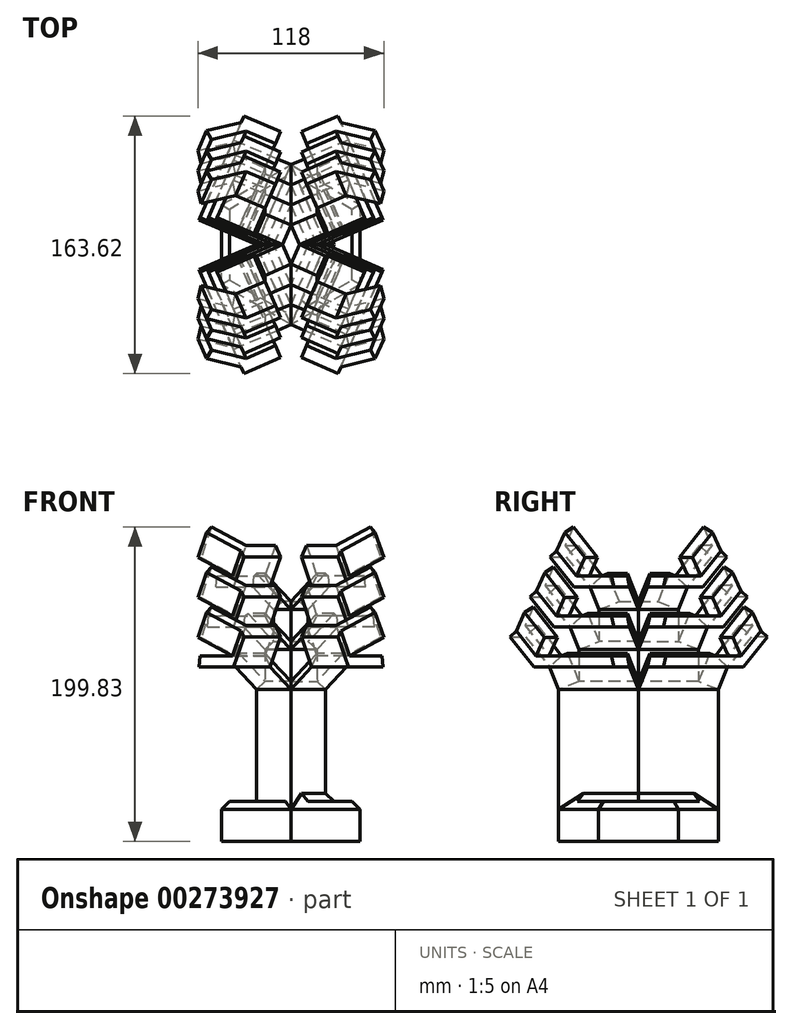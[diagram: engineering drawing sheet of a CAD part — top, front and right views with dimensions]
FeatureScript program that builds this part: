
annotation { "Feature Type Name" : "Feature", "Feature Type Description" : "" }
export const myFeature = defineFeature(function(context is Context, id is Id, definition is map)
    precondition{}
    {
        {
            var Q0;
            Q0=qCreatedBy(makeId("Top.planeOp"),FACE);
            var sketch = newSketch(context, id + "F0", { "sketchPlane" : qUnion([Q0])});
            skCircle(sketch, "E0.cCircle", {"center": v(0, 0) * mm, "radius": 43.95 * mm, "construction": true});
            skLineSegment(sketch, "E0.0", {"start": v(43.95, 25.37) * mm, "end": v(43.95, -25.37) * mm});
            skLineSegment(sketch, "E0.1", {"start": v(43.95, -25.37) * mm, "end": v(0, -50.74) * mm});
            skLineSegment(sketch, "E0.2", {"start": v(0, -50.74) * mm, "end": v(-43.95, -25.37) * mm});
            skLineSegment(sketch, "E0.3", {"start": v(-43.95, -25.37) * mm, "end": v(-43.95, 25.37) * mm});
            skLineSegment(sketch, "E0.4", {"start": v(-43.95, 25.37) * mm, "end": v(0, 50.74) * mm});
            skLineSegment(sketch, "E0.5", {"start": v(0, 50.74) * mm, "end": v(43.95, 25.37) * mm});
            skPoint(sketch, "E0.0.midPoint", {"position": v(43.95, 0) * mm});
            skLineSegment(sketch, "E1", {"start": v(-21.97, 0) * mm, "end": v(0, 0) * mm});
            skLineSegment(sketch, "E2", {"start": v(-21.97, 0) * mm, "end": v(0, -50.74) * mm});
            skLineSegment(sketch, "E3", {"start": v(0, 50.74) * mm, "end": v(-21.97, 0) * mm});
            skLineSegment(sketch, "E4", {"start": v(0, 0) * mm, "end": v(21.97, 0) * mm});
            skPoint(sketch, "E4.endSnap0", {"position": v(21.97, 38.06) * mm});
            skLineSegment(sketch, "E5", {"start": v(21.97, 0) * mm, "end": v(0, 50.74) * mm});
            skLineSegment(sketch, "E6", {"start": v(0, -50.74) * mm, "end": v(21.97, 0) * mm});
            skSolve(sketch);
        }
        {
            var Q0;
            Q0 = qSketchRegion(id + "F0", true);
            extrude(context, id + "F1", {"entities" : qUnion([Q0]), "depth" : 25.4 * mm});
        }
        {
            var Q0;
            Q0=makeQuery(id+"F1.opExtrude","CAP_FACE",FACE,{"disambiguationData":[OSD([sQuery(id+"F0.wireOp",EDGE,"E0.0"),sQuery(id+"F0.wireOp",EDGE,"E0.1"),sQuery(id+"F0.wireOp",EDGE,"E0.2"),sQuery(id+"F0.wireOp",EDGE,"E0.3"),sQuery(id+"F0.wireOp",EDGE,"E0.4"),sQuery(id+"F0.wireOp",EDGE,"E0.5")])],"isStart":false});
            var sketch = newSketch(context, id + "F2", { "sketchPlane" : qUnion([Q0])});
            skLineSegment(sketch, "E7", {"start": v(0, 50.74) * mm, "end": v(-21.97, 0) * mm});
            skPoint(sketch, "E7.endSnap0", {"position": v(-21.97, 38.06) * mm});
            skLineSegment(sketch, "E8", {"start": v(-21.97, 0) * mm, "end": v(0, -50.74) * mm});
            skLineSegment(sketch, "E9", {"start": v(0, -50.74) * mm, "end": v(21.97, 0) * mm});
            skPoint(sketch, "E9.endSnap0", {"position": v(21.97, -38.06) * mm});
            skLineSegment(sketch, "E10", {"start": v(21.97, 0) * mm, "end": v(0, 50.74) * mm});
            skSolve(sketch);
        }
        {
            var Q0;
            Q0 = qSketchRegion(id + "F2", true);
            extrude(context, id + "F3", {"entities" : qUnion([Q0]), "operationType" : NewBodyOperationType.ADD, "depth" : 25.4 * mm});
        }
        {
            var Q0;
            Q0=makeQuery(id+"F3.opExtrude","CAP_FACE",FACE,{"disambiguationData":[OSD([sQuery(id+"F2.wireOp",EDGE,"E7"),sQuery(id+"F2.wireOp",EDGE,"E8"),sQuery(id+"F2.wireOp",EDGE,"E9"),sQuery(id+"F2.wireOp",EDGE,"E10")])],"isStart":false});
            extrude(context, id + "F4", {"entities" : qUnion([Q0]), "operationType" : NewBodyOperationType.ADD, "depth" : 25.4 * mm});
        }
        {
            var Q0;
            Q0=makeQuery(id+"F4.opExtrude","CAP_FACE",FACE,{"disambiguationData":[OSD([sQuery(id+"F2.wireOp",EDGE,"E7"),sQuery(id+"F2.wireOp",EDGE,"E8"),sQuery(id+"F2.wireOp",EDGE,"E9"),sQuery(id+"F2.wireOp",EDGE,"E10")])],"isStart":false});
            extrude(context, id + "F5", {"entities" : qUnion([Q0]), "operationType" : NewBodyOperationType.ADD, "depth" : 25.4 * mm});
        }
        {
            var Q0;
            Q0=makeQuery(id+"F1.opExtrude","CAP_EDGE",EDGE,{"disambiguationData":[OSD([sQuery(id+"F0.wireOp",EDGE,"E0.0")])],"isStart":false});
            var Q1;
            Q1=makeQuery(id+"F1.opExtrude","CAP_EDGE",EDGE,{"disambiguationData":[OSD([sQuery(id+"F0.wireOp",EDGE,"E0.1")])],"isStart":false});
            var Q2;
            Q2=makeQuery(id+"F1.opExtrude","CAP_EDGE",EDGE,{"disambiguationData":[OSD([sQuery(id+"F0.wireOp",EDGE,"E0.5")])],"isStart":false});
            var Q3;
            Q3=makeQuery(id+"F1.opExtrude","CAP_EDGE",EDGE,{"disambiguationData":[OSD([sQuery(id+"F0.wireOp",EDGE,"E0.4")])],"isStart":false});
            var Q4;
            Q4=makeQuery(id+"F1.opExtrude","CAP_EDGE",EDGE,{"disambiguationData":[OSD([sQuery(id+"F0.wireOp",EDGE,"E0.3")])],"isStart":false});
            var Q5;
            Q5=makeQuery(id+"F1.opExtrude","CAP_EDGE",EDGE,{"disambiguationData":[OSD([sQuery(id+"F0.wireOp",EDGE,"E0.2")])],"isStart":false});
            chamfer(context, id + "F6", {"entities" : qUnion([Q0, Q1, Q2, Q3, Q4, Q5]), "width" : 5.08 * mm, "tangentPropagation" : true});
        }
        {
            var Q0;
            Q0=makeQuery(id+"F3.opExtrude","CAP_EDGE",EDGE,{"disambiguationData":[OSD([sQuery(id+"F2.wireOp",EDGE,"E10")])],"isStart":true});
            var Q1;
            Q1=makeQuery(id+"F3.opExtrude","CAP_EDGE",EDGE,{"disambiguationData":[OSD([sQuery(id+"F2.wireOp",EDGE,"E9")])],"isStart":true});
            var Q2;
            Q2=makeQuery(id+"F3.opExtrude","CAP_EDGE",EDGE,{"disambiguationData":[OSD([sQuery(id+"F2.wireOp",EDGE,"E7")])],"isStart":true});
            var Q3;
            Q3=makeQuery(id+"F3.opExtrude","CAP_EDGE",EDGE,{"disambiguationData":[OSD([sQuery(id+"F2.wireOp",EDGE,"E8")])],"isStart":true});
            chamfer(context, id + "F7", {"entities" : qUnion([Q0, Q1, Q2, Q3]), "width" : 5.08 * mm, "tangentPropagation" : true});
        }
        {
            var Q0;
            Q0=makeQuery(id+"F5.opExtrude","CAP_FACE",FACE,{"disambiguationData":[OSD([sQuery(id+"F2.wireOp",EDGE,"E7"),sQuery(id+"F2.wireOp",EDGE,"E8"),sQuery(id+"F2.wireOp",EDGE,"E9"),sQuery(id+"F2.wireOp",EDGE,"E10")])],"isStart":false});
            chamfer(context, id + "F8", {"entities" : qUnion([Q0]), "width" : 5.08 * mm, "tangentPropagation" : true});
        }
        {
            var Q0;
            Q0=makeQuery(id+"F5.opExtrude","CAP_FACE",FACE,{"disambiguationData":[OSD([sQuery(id+"F2.wireOp",EDGE,"E7"),sQuery(id+"F2.wireOp",EDGE,"E8"),sQuery(id+"F2.wireOp",EDGE,"E9"),sQuery(id+"F2.wireOp",EDGE,"E10")])],"isStart":false});
            extrude(context, id + "F9", {"entities" : qUnion([Q0]), "operationType" : NewBodyOperationType.ADD, "depth" : 25.4 * mm});
        }
        {
            var Q0;
            Q0=makeQuery(id+"F9.opExtrude","CAP_FACE",FACE,{"disambiguationData":[OSD([sQuery(id+"F2.wireOp",EDGE,"E7"),sQuery(id+"F2.wireOp",EDGE,"E8"),sQuery(id+"F2.wireOp",EDGE,"E9"),sQuery(id+"F2.wireOp",EDGE,"E10")])],"isStart":false});
            chamfer(context, id + "F10", {"entities" : qUnion([Q0]), "width" : 5.08 * mm, "tangentPropagation" : true});
        }
        {
            var Q0;
            Q0=makeQuery(id+"F9.opExtrude","CAP_FACE",FACE,{"disambiguationData":[OSD([sQuery(id+"F2.wireOp",EDGE,"E7"),sQuery(id+"F2.wireOp",EDGE,"E8"),sQuery(id+"F2.wireOp",EDGE,"E9"),sQuery(id+"F2.wireOp",EDGE,"E10")])],"isStart":false});
            extrude(context, id + "F11", {"entities" : qUnion([Q0]), "operationType" : NewBodyOperationType.ADD, "depth" : 25.4 * mm});
        }
        {
            var Q0;
            Q0=makeQuery(id+"F11.opExtrude","CAP_FACE",FACE,{"disambiguationData":[OSD([sQuery(id+"F2.wireOp",EDGE,"E7"),sQuery(id+"F2.wireOp",EDGE,"E8"),sQuery(id+"F2.wireOp",EDGE,"E9"),sQuery(id+"F2.wireOp",EDGE,"E10")])],"isStart":false});
            chamfer(context, id + "F12", {"entities" : qUnion([Q0]), "width" : 5.08 * mm, "tangentPropagation" : true});
        }
        {
            var Q0;
            Q0=makeQuery(id+"F8.opChamfer","BLEND_FACE",FACE,{"disambiguationData":[OSD([sQuery(id+"F2.wireOp",EDGE,"E10")])]});
            var Q1;
            {var subQ0=sQuery(id+"F2.wireOp",EDGE,"E10");var subQ1=sQuery(id+"F2.wireOp",EDGE,"E9");var subQ2=sQuery(id+"F2.wireOp",EDGE,"E8");var subQ3=sQuery(id+"F2.wireOp",EDGE,"E7");Q1=makeQuery(id+"F10.opChamfer","BLEND_FACE",FACE,{"disambiguationData":[OSD([subQ3,subQ2,subQ1,subQ0]),TDD([makeQuery(id+"F9.opExtrude","CAP_EDGE",EDGE,{"disambiguationData":[OSD([subQ3,subQ2,subQ1,subQ0]),TDD([makeQuery(id+"F8.opChamfer","BLEND_EDGE",EDGE,{"blendedFrom":[makeQuery(id+"F5.opExtrude","CAP_EDGE",EDGE,{"disambiguationData":[OSD([subQ0])],"isStart":false}),makeQuery(id+"F5.opExtrude","CAP_FACE",FACE,{"disambiguationData":[OSD([subQ3,subQ2,subQ1,subQ0])],"isStart":false})],"blendedInto":[makeQuery(id+"F5.opExtrude","CAP_FACE",FACE,{"disambiguationData":[OSD([subQ3,subQ2,subQ1,subQ0])],"isStart":false})]})])],"isStart":false})])]});}
            var Q2;
            {var subQ0=sQuery(id+"F2.wireOp",EDGE,"E10");var subQ1=sQuery(id+"F2.wireOp",EDGE,"E9");var subQ2=sQuery(id+"F2.wireOp",EDGE,"E8");var subQ3=sQuery(id+"F2.wireOp",EDGE,"E7");Q2=makeQuery(id+"F12.opChamfer","BLEND_FACE",FACE,{"disambiguationData":[OSD([subQ3,subQ2,subQ1,subQ0]),TDD([makeQuery(id+"F11.opExtrude","CAP_EDGE",EDGE,{"disambiguationData":[OSD([subQ3,subQ2,subQ1,subQ0]),TDD([makeQuery(id+"F10.opChamfer","BLEND_EDGE",EDGE,{"blendedFrom":[makeQuery(id+"F9.opExtrude","CAP_EDGE",EDGE,{"disambiguationData":[OSD([subQ3,subQ2,subQ1,subQ0]),TDD([makeQuery(id+"F8.opChamfer","BLEND_EDGE",EDGE,{"blendedFrom":[makeQuery(id+"F5.opExtrude","CAP_EDGE",EDGE,{"disambiguationData":[OSD([subQ0])],"isStart":false}),makeQuery(id+"F5.opExtrude","CAP_FACE",FACE,{"disambiguationData":[OSD([subQ3,subQ2,subQ1,subQ0])],"isStart":false})],"blendedInto":[makeQuery(id+"F5.opExtrude","CAP_FACE",FACE,{"disambiguationData":[OSD([subQ3,subQ2,subQ1,subQ0])],"isStart":false})]})])],"isStart":false}),makeQuery(id+"F9.opExtrude","CAP_FACE",FACE,{"disambiguationData":[OSD([subQ3,subQ2,subQ1,subQ0])],"isStart":false})],"blendedInto":[makeQuery(id+"F9.opExtrude","CAP_FACE",FACE,{"disambiguationData":[OSD([subQ3,subQ2,subQ1,subQ0])],"isStart":false})]})])],"isStart":false})])]});}
            extrude(context, id + "F13", {"entities" : qUnion([Q0, Q1, Q2]), "operationType" : NewBodyOperationType.ADD, "depth" : 25.4 * mm});
        }
        {
            var Q0;
            Q0=makeQuery(id+"F8.opChamfer","BLEND_FACE",FACE,{"disambiguationData":[OSD([sQuery(id+"F2.wireOp",EDGE,"E9")])]});
            var Q1;
            {var subQ0=sQuery(id+"F2.wireOp",EDGE,"E10");var subQ1=sQuery(id+"F2.wireOp",EDGE,"E9");var subQ2=sQuery(id+"F2.wireOp",EDGE,"E8");var subQ3=sQuery(id+"F2.wireOp",EDGE,"E7");Q1=makeQuery(id+"F10.opChamfer","BLEND_FACE",FACE,{"disambiguationData":[OSD([subQ3,subQ2,subQ1,subQ0]),TDD([makeQuery(id+"F9.opExtrude","CAP_EDGE",EDGE,{"disambiguationData":[OSD([subQ3,subQ2,subQ1,subQ0]),TDD([makeQuery(id+"F8.opChamfer","BLEND_EDGE",EDGE,{"blendedFrom":[makeQuery(id+"F5.opExtrude","CAP_EDGE",EDGE,{"disambiguationData":[OSD([subQ1])],"isStart":false}),makeQuery(id+"F5.opExtrude","CAP_FACE",FACE,{"disambiguationData":[OSD([subQ3,subQ2,subQ1,subQ0])],"isStart":false})],"blendedInto":[makeQuery(id+"F5.opExtrude","CAP_FACE",FACE,{"disambiguationData":[OSD([subQ3,subQ2,subQ1,subQ0])],"isStart":false})]})])],"isStart":false})])]});}
            var Q2;
            {var subQ0=sQuery(id+"F2.wireOp",EDGE,"E10");var subQ1=sQuery(id+"F2.wireOp",EDGE,"E9");var subQ2=sQuery(id+"F2.wireOp",EDGE,"E8");var subQ3=sQuery(id+"F2.wireOp",EDGE,"E7");Q2=makeQuery(id+"F12.opChamfer","BLEND_FACE",FACE,{"disambiguationData":[OSD([subQ3,subQ2,subQ1,subQ0]),TDD([makeQuery(id+"F11.opExtrude","CAP_EDGE",EDGE,{"disambiguationData":[OSD([subQ3,subQ2,subQ1,subQ0]),TDD([makeQuery(id+"F10.opChamfer","BLEND_EDGE",EDGE,{"blendedFrom":[makeQuery(id+"F9.opExtrude","CAP_EDGE",EDGE,{"disambiguationData":[OSD([subQ3,subQ2,subQ1,subQ0]),TDD([makeQuery(id+"F8.opChamfer","BLEND_EDGE",EDGE,{"blendedFrom":[makeQuery(id+"F5.opExtrude","CAP_EDGE",EDGE,{"disambiguationData":[OSD([subQ1])],"isStart":false}),makeQuery(id+"F5.opExtrude","CAP_FACE",FACE,{"disambiguationData":[OSD([subQ3,subQ2,subQ1,subQ0])],"isStart":false})],"blendedInto":[makeQuery(id+"F5.opExtrude","CAP_FACE",FACE,{"disambiguationData":[OSD([subQ3,subQ2,subQ1,subQ0])],"isStart":false})]})])],"isStart":false}),makeQuery(id+"F9.opExtrude","CAP_FACE",FACE,{"disambiguationData":[OSD([subQ3,subQ2,subQ1,subQ0])],"isStart":false})],"blendedInto":[makeQuery(id+"F9.opExtrude","CAP_FACE",FACE,{"disambiguationData":[OSD([subQ3,subQ2,subQ1,subQ0])],"isStart":false})]})])],"isStart":false})])]});}
            extrude(context, id + "F14", {"entities" : qUnion([Q0, Q1, Q2]), "operationType" : NewBodyOperationType.ADD, "depth" : 25.4 * mm});
        }
        {
            var Q0;
            Q0=makeQuery(id+"F8.opChamfer","BLEND_FACE",FACE,{"disambiguationData":[OSD([sQuery(id+"F2.wireOp",EDGE,"E7")])]});
            var Q1;
            {var subQ0=sQuery(id+"F2.wireOp",EDGE,"E10");var subQ1=sQuery(id+"F2.wireOp",EDGE,"E9");var subQ2=sQuery(id+"F2.wireOp",EDGE,"E8");var subQ3=sQuery(id+"F2.wireOp",EDGE,"E7");Q1=makeQuery(id+"F10.opChamfer","BLEND_FACE",FACE,{"disambiguationData":[OSD([subQ3,subQ2,subQ1,subQ0]),TDD([makeQuery(id+"F9.opExtrude","CAP_EDGE",EDGE,{"disambiguationData":[OSD([subQ3,subQ2,subQ1,subQ0]),TDD([makeQuery(id+"F8.opChamfer","BLEND_EDGE",EDGE,{"blendedFrom":[makeQuery(id+"F5.opExtrude","CAP_EDGE",EDGE,{"disambiguationData":[OSD([subQ3])],"isStart":false}),makeQuery(id+"F5.opExtrude","CAP_FACE",FACE,{"disambiguationData":[OSD([subQ3,subQ2,subQ1,subQ0])],"isStart":false})],"blendedInto":[makeQuery(id+"F5.opExtrude","CAP_FACE",FACE,{"disambiguationData":[OSD([subQ3,subQ2,subQ1,subQ0])],"isStart":false})]})])],"isStart":false})])]});}
            var Q2;
            {var subQ0=sQuery(id+"F2.wireOp",EDGE,"E10");var subQ1=sQuery(id+"F2.wireOp",EDGE,"E9");var subQ2=sQuery(id+"F2.wireOp",EDGE,"E8");var subQ3=sQuery(id+"F2.wireOp",EDGE,"E7");Q2=makeQuery(id+"F12.opChamfer","BLEND_FACE",FACE,{"disambiguationData":[OSD([subQ3,subQ2,subQ1,subQ0]),TDD([makeQuery(id+"F11.opExtrude","CAP_EDGE",EDGE,{"disambiguationData":[OSD([subQ3,subQ2,subQ1,subQ0]),TDD([makeQuery(id+"F10.opChamfer","BLEND_EDGE",EDGE,{"blendedFrom":[makeQuery(id+"F9.opExtrude","CAP_EDGE",EDGE,{"disambiguationData":[OSD([subQ3,subQ2,subQ1,subQ0]),TDD([makeQuery(id+"F8.opChamfer","BLEND_EDGE",EDGE,{"blendedFrom":[makeQuery(id+"F5.opExtrude","CAP_EDGE",EDGE,{"disambiguationData":[OSD([subQ3])],"isStart":false}),makeQuery(id+"F5.opExtrude","CAP_FACE",FACE,{"disambiguationData":[OSD([subQ3,subQ2,subQ1,subQ0])],"isStart":false})],"blendedInto":[makeQuery(id+"F5.opExtrude","CAP_FACE",FACE,{"disambiguationData":[OSD([subQ3,subQ2,subQ1,subQ0])],"isStart":false})]})])],"isStart":false}),makeQuery(id+"F9.opExtrude","CAP_FACE",FACE,{"disambiguationData":[OSD([subQ3,subQ2,subQ1,subQ0])],"isStart":false})],"blendedInto":[makeQuery(id+"F9.opExtrude","CAP_FACE",FACE,{"disambiguationData":[OSD([subQ3,subQ2,subQ1,subQ0])],"isStart":false})]})])],"isStart":false})])]});}
            extrude(context, id + "F15", {"entities" : qUnion([Q0, Q1, Q2]), "operationType" : NewBodyOperationType.ADD, "depth" : 25.4 * mm});
        }
        {
            var Q0;
            Q0=makeQuery(id+"F8.opChamfer","BLEND_FACE",FACE,{"disambiguationData":[OSD([sQuery(id+"F2.wireOp",EDGE,"E8")])]});
            var Q1;
            {var subQ0=sQuery(id+"F2.wireOp",EDGE,"E10");var subQ1=sQuery(id+"F2.wireOp",EDGE,"E9");var subQ2=sQuery(id+"F2.wireOp",EDGE,"E8");var subQ3=sQuery(id+"F2.wireOp",EDGE,"E7");Q1=makeQuery(id+"F10.opChamfer","BLEND_FACE",FACE,{"disambiguationData":[OSD([subQ3,subQ2,subQ1,subQ0]),TDD([makeQuery(id+"F9.opExtrude","CAP_EDGE",EDGE,{"disambiguationData":[OSD([subQ3,subQ2,subQ1,subQ0]),TDD([makeQuery(id+"F8.opChamfer","BLEND_EDGE",EDGE,{"blendedFrom":[makeQuery(id+"F5.opExtrude","CAP_EDGE",EDGE,{"disambiguationData":[OSD([subQ2])],"isStart":false}),makeQuery(id+"F5.opExtrude","CAP_FACE",FACE,{"disambiguationData":[OSD([subQ3,subQ2,subQ1,subQ0])],"isStart":false})],"blendedInto":[makeQuery(id+"F5.opExtrude","CAP_FACE",FACE,{"disambiguationData":[OSD([subQ3,subQ2,subQ1,subQ0])],"isStart":false})]})])],"isStart":false})])]});}
            var Q2;
            {var subQ0=sQuery(id+"F2.wireOp",EDGE,"E10");var subQ1=sQuery(id+"F2.wireOp",EDGE,"E9");var subQ2=sQuery(id+"F2.wireOp",EDGE,"E8");var subQ3=sQuery(id+"F2.wireOp",EDGE,"E7");Q2=makeQuery(id+"F12.opChamfer","BLEND_FACE",FACE,{"disambiguationData":[OSD([subQ3,subQ2,subQ1,subQ0]),TDD([makeQuery(id+"F11.opExtrude","CAP_EDGE",EDGE,{"disambiguationData":[OSD([subQ3,subQ2,subQ1,subQ0]),TDD([makeQuery(id+"F10.opChamfer","BLEND_EDGE",EDGE,{"blendedFrom":[makeQuery(id+"F9.opExtrude","CAP_EDGE",EDGE,{"disambiguationData":[OSD([subQ3,subQ2,subQ1,subQ0]),TDD([makeQuery(id+"F8.opChamfer","BLEND_EDGE",EDGE,{"blendedFrom":[makeQuery(id+"F5.opExtrude","CAP_EDGE",EDGE,{"disambiguationData":[OSD([subQ2])],"isStart":false}),makeQuery(id+"F5.opExtrude","CAP_FACE",FACE,{"disambiguationData":[OSD([subQ3,subQ2,subQ1,subQ0])],"isStart":false})],"blendedInto":[makeQuery(id+"F5.opExtrude","CAP_FACE",FACE,{"disambiguationData":[OSD([subQ3,subQ2,subQ1,subQ0])],"isStart":false})]})])],"isStart":false}),makeQuery(id+"F9.opExtrude","CAP_FACE",FACE,{"disambiguationData":[OSD([subQ3,subQ2,subQ1,subQ0])],"isStart":false})],"blendedInto":[makeQuery(id+"F9.opExtrude","CAP_FACE",FACE,{"disambiguationData":[OSD([subQ3,subQ2,subQ1,subQ0])],"isStart":false})]})])],"isStart":false})])]});}
            extrude(context, id + "F16", {"entities" : qUnion([Q0, Q1, Q2]), "operationType" : NewBodyOperationType.ADD, "depth" : 25.4 * mm});
        }
        {
            var Q0;
            {var subQ0=sQuery(id+"F2.wireOp",EDGE,"E10");var subQ1=sQuery(id+"F2.wireOp",EDGE,"E9");var subQ2=sQuery(id+"F2.wireOp",EDGE,"E8");var subQ3=sQuery(id+"F2.wireOp",EDGE,"E7");var subQ4=makeQuery(id+"F10.opChamfer","BLEND_EDGE",EDGE,{"blendedFrom":[makeQuery(id+"F9.opExtrude","CAP_EDGE",EDGE,{"disambiguationData":[OSD([subQ3,subQ2,subQ1,subQ0]),TDD([makeQuery(id+"F8.opChamfer","BLEND_EDGE",EDGE,{"blendedFrom":[makeQuery(id+"F5.opExtrude","CAP_EDGE",EDGE,{"disambiguationData":[OSD([subQ3])],"isStart":false}),makeQuery(id+"F5.opExtrude","CAP_FACE",FACE,{"disambiguationData":[OSD([subQ3,subQ2,subQ1,subQ0])],"isStart":false})],"blendedInto":[makeQuery(id+"F5.opExtrude","CAP_FACE",FACE,{"disambiguationData":[OSD([subQ3,subQ2,subQ1,subQ0])],"isStart":false})]})])],"isStart":false}),makeQuery(id+"F9.opExtrude","CAP_FACE",FACE,{"disambiguationData":[OSD([subQ3,subQ2,subQ1,subQ0])],"isStart":false})],"blendedInto":[makeQuery(id+"F9.opExtrude","CAP_FACE",FACE,{"disambiguationData":[OSD([subQ3,subQ2,subQ1,subQ0])],"isStart":false})]});Q0=makeQuery(id+"F15.opExtrude","CAP_EDGE",EDGE,{"disambiguationData":[OSD([subQ3,subQ2,subQ1,subQ0]),TDD([makeQuery(id+"F12.opChamfer","BLEND_EDGE",EDGE,{"blendedFrom":[makeQuery(id+"F11.opExtrude","CAP_EDGE",EDGE,{"disambiguationData":[OSD([subQ3,subQ2,subQ1,subQ0]),TDD([subQ4])],"isStart":false}),makeQuery(id+"F11.opExtrude","SWEPT_FACE",FACE,{"disambiguationData":[OSD([subQ3,subQ2,subQ1,subQ0]),TDD([subQ4])]})],"blendedInto":[makeQuery(id+"F11.opExtrude","SWEPT_FACE",FACE,{"disambiguationData":[OSD([subQ3,subQ2,subQ1,subQ0]),TDD([subQ4])]})]})])],"isStart":false});}
            var Q1;
            {var subQ0=sQuery(id+"F2.wireOp",EDGE,"E10");var subQ1=sQuery(id+"F2.wireOp",EDGE,"E9");var subQ2=sQuery(id+"F2.wireOp",EDGE,"E8");var subQ3=sQuery(id+"F2.wireOp",EDGE,"E7");var subQ4=makeQuery(id+"F8.opChamfer","BLEND_EDGE",EDGE,{"blendedFrom":[makeQuery(id+"F5.opExtrude","CAP_EDGE",EDGE,{"disambiguationData":[OSD([subQ3])],"isStart":false}),makeQuery(id+"F5.opExtrude","CAP_FACE",FACE,{"disambiguationData":[OSD([subQ3,subQ2,subQ1,subQ0])],"isStart":false})],"blendedInto":[makeQuery(id+"F5.opExtrude","CAP_FACE",FACE,{"disambiguationData":[OSD([subQ3,subQ2,subQ1,subQ0])],"isStart":false})]});Q1=makeQuery(id+"F15.opExtrude","CAP_EDGE",EDGE,{"disambiguationData":[OSD([subQ3,subQ2,subQ1,subQ0]),TDD([makeQuery(id+"F10.opChamfer","BLEND_EDGE",EDGE,{"blendedFrom":[makeQuery(id+"F9.opExtrude","CAP_EDGE",EDGE,{"disambiguationData":[OSD([subQ3,subQ2,subQ1,subQ0]),TDD([subQ4])],"isStart":false}),makeQuery(id+"F9.opExtrude","SWEPT_FACE",FACE,{"disambiguationData":[OSD([subQ3,subQ2,subQ1,subQ0]),TDD([subQ4])]})],"blendedInto":[makeQuery(id+"F9.opExtrude","SWEPT_FACE",FACE,{"disambiguationData":[OSD([subQ3,subQ2,subQ1,subQ0]),TDD([subQ4])]})]})])],"isStart":false});}
            var Q2;
            Q2=makeQuery(id+"F15.opExtrude","CAP_EDGE",EDGE,{"disambiguationData":[OSD([sQuery(id+"F2.wireOp",EDGE,"E7")])],"isStart":false});
            var Q3;
            Q3=makeQuery(id+"F16.opExtrude","CAP_EDGE",EDGE,{"disambiguationData":[OSD([sQuery(id+"F2.wireOp",EDGE,"E8")])],"isStart":false});
            var Q4;
            {var subQ0=sQuery(id+"F2.wireOp",EDGE,"E10");var subQ1=sQuery(id+"F2.wireOp",EDGE,"E9");var subQ2=sQuery(id+"F2.wireOp",EDGE,"E8");var subQ3=sQuery(id+"F2.wireOp",EDGE,"E7");var subQ4=makeQuery(id+"F8.opChamfer","BLEND_EDGE",EDGE,{"blendedFrom":[makeQuery(id+"F5.opExtrude","CAP_EDGE",EDGE,{"disambiguationData":[OSD([subQ2])],"isStart":false}),makeQuery(id+"F5.opExtrude","CAP_FACE",FACE,{"disambiguationData":[OSD([subQ3,subQ2,subQ1,subQ0])],"isStart":false})],"blendedInto":[makeQuery(id+"F5.opExtrude","CAP_FACE",FACE,{"disambiguationData":[OSD([subQ3,subQ2,subQ1,subQ0])],"isStart":false})]});Q4=makeQuery(id+"F16.opExtrude","CAP_EDGE",EDGE,{"disambiguationData":[OSD([subQ3,subQ2,subQ1,subQ0]),TDD([makeQuery(id+"F10.opChamfer","BLEND_EDGE",EDGE,{"blendedFrom":[makeQuery(id+"F9.opExtrude","CAP_EDGE",EDGE,{"disambiguationData":[OSD([subQ3,subQ2,subQ1,subQ0]),TDD([subQ4])],"isStart":false}),makeQuery(id+"F9.opExtrude","SWEPT_FACE",FACE,{"disambiguationData":[OSD([subQ3,subQ2,subQ1,subQ0]),TDD([subQ4])]})],"blendedInto":[makeQuery(id+"F9.opExtrude","SWEPT_FACE",FACE,{"disambiguationData":[OSD([subQ3,subQ2,subQ1,subQ0]),TDD([subQ4])]})]})])],"isStart":false});}
            var Q5;
            {var subQ0=sQuery(id+"F2.wireOp",EDGE,"E10");var subQ1=sQuery(id+"F2.wireOp",EDGE,"E9");var subQ2=sQuery(id+"F2.wireOp",EDGE,"E8");var subQ3=sQuery(id+"F2.wireOp",EDGE,"E7");var subQ4=makeQuery(id+"F10.opChamfer","BLEND_EDGE",EDGE,{"blendedFrom":[makeQuery(id+"F9.opExtrude","CAP_EDGE",EDGE,{"disambiguationData":[OSD([subQ3,subQ2,subQ1,subQ0]),TDD([makeQuery(id+"F8.opChamfer","BLEND_EDGE",EDGE,{"blendedFrom":[makeQuery(id+"F5.opExtrude","CAP_EDGE",EDGE,{"disambiguationData":[OSD([subQ2])],"isStart":false}),makeQuery(id+"F5.opExtrude","CAP_FACE",FACE,{"disambiguationData":[OSD([subQ3,subQ2,subQ1,subQ0])],"isStart":false})],"blendedInto":[makeQuery(id+"F5.opExtrude","CAP_FACE",FACE,{"disambiguationData":[OSD([subQ3,subQ2,subQ1,subQ0])],"isStart":false})]})])],"isStart":false}),makeQuery(id+"F9.opExtrude","CAP_FACE",FACE,{"disambiguationData":[OSD([subQ3,subQ2,subQ1,subQ0])],"isStart":false})],"blendedInto":[makeQuery(id+"F9.opExtrude","CAP_FACE",FACE,{"disambiguationData":[OSD([subQ3,subQ2,subQ1,subQ0])],"isStart":false})]});Q5=makeQuery(id+"F16.opExtrude","CAP_EDGE",EDGE,{"disambiguationData":[OSD([subQ3,subQ2,subQ1,subQ0]),TDD([makeQuery(id+"F12.opChamfer","BLEND_EDGE",EDGE,{"blendedFrom":[makeQuery(id+"F11.opExtrude","CAP_EDGE",EDGE,{"disambiguationData":[OSD([subQ3,subQ2,subQ1,subQ0]),TDD([subQ4])],"isStart":false}),makeQuery(id+"F11.opExtrude","SWEPT_FACE",FACE,{"disambiguationData":[OSD([subQ3,subQ2,subQ1,subQ0]),TDD([subQ4])]})],"blendedInto":[makeQuery(id+"F11.opExtrude","SWEPT_FACE",FACE,{"disambiguationData":[OSD([subQ3,subQ2,subQ1,subQ0]),TDD([subQ4])]})]})])],"isStart":false});}
            var Q6;
            Q6=makeQuery(id+"F13.opExtrude","CAP_EDGE",EDGE,{"disambiguationData":[OSD([sQuery(id+"F2.wireOp",EDGE,"E10")])],"isStart":false});
            var Q7;
            Q7=makeQuery(id+"F14.opExtrude","CAP_EDGE",EDGE,{"disambiguationData":[OSD([sQuery(id+"F2.wireOp",EDGE,"E9")])],"isStart":false});
            var Q8;
            {var subQ0=sQuery(id+"F2.wireOp",EDGE,"E10");var subQ1=sQuery(id+"F2.wireOp",EDGE,"E9");var subQ2=sQuery(id+"F2.wireOp",EDGE,"E8");var subQ3=sQuery(id+"F2.wireOp",EDGE,"E7");var subQ4=makeQuery(id+"F8.opChamfer","BLEND_EDGE",EDGE,{"blendedFrom":[makeQuery(id+"F5.opExtrude","CAP_EDGE",EDGE,{"disambiguationData":[OSD([subQ1])],"isStart":false}),makeQuery(id+"F5.opExtrude","CAP_FACE",FACE,{"disambiguationData":[OSD([subQ3,subQ2,subQ1,subQ0])],"isStart":false})],"blendedInto":[makeQuery(id+"F5.opExtrude","CAP_FACE",FACE,{"disambiguationData":[OSD([subQ3,subQ2,subQ1,subQ0])],"isStart":false})]});Q8=makeQuery(id+"F14.opExtrude","CAP_EDGE",EDGE,{"disambiguationData":[OSD([subQ3,subQ2,subQ1,subQ0]),TDD([makeQuery(id+"F10.opChamfer","BLEND_EDGE",EDGE,{"blendedFrom":[makeQuery(id+"F9.opExtrude","CAP_EDGE",EDGE,{"disambiguationData":[OSD([subQ3,subQ2,subQ1,subQ0]),TDD([subQ4])],"isStart":false}),makeQuery(id+"F9.opExtrude","SWEPT_FACE",FACE,{"disambiguationData":[OSD([subQ3,subQ2,subQ1,subQ0]),TDD([subQ4])]})],"blendedInto":[makeQuery(id+"F9.opExtrude","SWEPT_FACE",FACE,{"disambiguationData":[OSD([subQ3,subQ2,subQ1,subQ0]),TDD([subQ4])]})]})])],"isStart":false});}
            var Q9;
            {var subQ0=sQuery(id+"F2.wireOp",EDGE,"E10");var subQ1=sQuery(id+"F2.wireOp",EDGE,"E9");var subQ2=sQuery(id+"F2.wireOp",EDGE,"E8");var subQ3=sQuery(id+"F2.wireOp",EDGE,"E7");var subQ4=makeQuery(id+"F8.opChamfer","BLEND_EDGE",EDGE,{"blendedFrom":[makeQuery(id+"F5.opExtrude","CAP_EDGE",EDGE,{"disambiguationData":[OSD([subQ0])],"isStart":false}),makeQuery(id+"F5.opExtrude","CAP_FACE",FACE,{"disambiguationData":[OSD([subQ3,subQ2,subQ1,subQ0])],"isStart":false})],"blendedInto":[makeQuery(id+"F5.opExtrude","CAP_FACE",FACE,{"disambiguationData":[OSD([subQ3,subQ2,subQ1,subQ0])],"isStart":false})]});Q9=makeQuery(id+"F13.opExtrude","CAP_EDGE",EDGE,{"disambiguationData":[OSD([subQ3,subQ2,subQ1,subQ0]),TDD([makeQuery(id+"F10.opChamfer","BLEND_EDGE",EDGE,{"blendedFrom":[makeQuery(id+"F9.opExtrude","CAP_EDGE",EDGE,{"disambiguationData":[OSD([subQ3,subQ2,subQ1,subQ0]),TDD([subQ4])],"isStart":false}),makeQuery(id+"F9.opExtrude","SWEPT_FACE",FACE,{"disambiguationData":[OSD([subQ3,subQ2,subQ1,subQ0]),TDD([subQ4])]})],"blendedInto":[makeQuery(id+"F9.opExtrude","SWEPT_FACE",FACE,{"disambiguationData":[OSD([subQ3,subQ2,subQ1,subQ0]),TDD([subQ4])]})]})])],"isStart":false});}
            var Q10;
            {var subQ0=sQuery(id+"F2.wireOp",EDGE,"E10");var subQ1=sQuery(id+"F2.wireOp",EDGE,"E9");var subQ2=sQuery(id+"F2.wireOp",EDGE,"E8");var subQ3=sQuery(id+"F2.wireOp",EDGE,"E7");var subQ4=makeQuery(id+"F10.opChamfer","BLEND_EDGE",EDGE,{"blendedFrom":[makeQuery(id+"F9.opExtrude","CAP_EDGE",EDGE,{"disambiguationData":[OSD([subQ3,subQ2,subQ1,subQ0]),TDD([makeQuery(id+"F8.opChamfer","BLEND_EDGE",EDGE,{"blendedFrom":[makeQuery(id+"F5.opExtrude","CAP_EDGE",EDGE,{"disambiguationData":[OSD([subQ0])],"isStart":false}),makeQuery(id+"F5.opExtrude","CAP_FACE",FACE,{"disambiguationData":[OSD([subQ3,subQ2,subQ1,subQ0])],"isStart":false})],"blendedInto":[makeQuery(id+"F5.opExtrude","CAP_FACE",FACE,{"disambiguationData":[OSD([subQ3,subQ2,subQ1,subQ0])],"isStart":false})]})])],"isStart":false}),makeQuery(id+"F9.opExtrude","CAP_FACE",FACE,{"disambiguationData":[OSD([subQ3,subQ2,subQ1,subQ0])],"isStart":false})],"blendedInto":[makeQuery(id+"F9.opExtrude","CAP_FACE",FACE,{"disambiguationData":[OSD([subQ3,subQ2,subQ1,subQ0])],"isStart":false})]});Q10=makeQuery(id+"F13.opExtrude","CAP_EDGE",EDGE,{"disambiguationData":[OSD([subQ3,subQ2,subQ1,subQ0]),TDD([makeQuery(id+"F12.opChamfer","BLEND_EDGE",EDGE,{"blendedFrom":[makeQuery(id+"F11.opExtrude","CAP_EDGE",EDGE,{"disambiguationData":[OSD([subQ3,subQ2,subQ1,subQ0]),TDD([subQ4])],"isStart":false}),makeQuery(id+"F11.opExtrude","SWEPT_FACE",FACE,{"disambiguationData":[OSD([subQ3,subQ2,subQ1,subQ0]),TDD([subQ4])]})],"blendedInto":[makeQuery(id+"F11.opExtrude","SWEPT_FACE",FACE,{"disambiguationData":[OSD([subQ3,subQ2,subQ1,subQ0]),TDD([subQ4])]})]})])],"isStart":false});}
            var Q11;
            {var subQ0=sQuery(id+"F2.wireOp",EDGE,"E10");var subQ1=sQuery(id+"F2.wireOp",EDGE,"E9");var subQ2=sQuery(id+"F2.wireOp",EDGE,"E8");var subQ3=sQuery(id+"F2.wireOp",EDGE,"E7");var subQ4=makeQuery(id+"F10.opChamfer","BLEND_EDGE",EDGE,{"blendedFrom":[makeQuery(id+"F9.opExtrude","CAP_EDGE",EDGE,{"disambiguationData":[OSD([subQ3,subQ2,subQ1,subQ0]),TDD([makeQuery(id+"F8.opChamfer","BLEND_EDGE",EDGE,{"blendedFrom":[makeQuery(id+"F5.opExtrude","CAP_EDGE",EDGE,{"disambiguationData":[OSD([subQ1])],"isStart":false}),makeQuery(id+"F5.opExtrude","CAP_FACE",FACE,{"disambiguationData":[OSD([subQ3,subQ2,subQ1,subQ0])],"isStart":false})],"blendedInto":[makeQuery(id+"F5.opExtrude","CAP_FACE",FACE,{"disambiguationData":[OSD([subQ3,subQ2,subQ1,subQ0])],"isStart":false})]})])],"isStart":false}),makeQuery(id+"F9.opExtrude","CAP_FACE",FACE,{"disambiguationData":[OSD([subQ3,subQ2,subQ1,subQ0])],"isStart":false})],"blendedInto":[makeQuery(id+"F9.opExtrude","CAP_FACE",FACE,{"disambiguationData":[OSD([subQ3,subQ2,subQ1,subQ0])],"isStart":false})]});Q11=makeQuery(id+"F14.opExtrude","CAP_EDGE",EDGE,{"disambiguationData":[OSD([subQ3,subQ2,subQ1,subQ0]),TDD([makeQuery(id+"F12.opChamfer","BLEND_EDGE",EDGE,{"blendedFrom":[makeQuery(id+"F11.opExtrude","CAP_EDGE",EDGE,{"disambiguationData":[OSD([subQ3,subQ2,subQ1,subQ0]),TDD([subQ4])],"isStart":false}),makeQuery(id+"F11.opExtrude","SWEPT_FACE",FACE,{"disambiguationData":[OSD([subQ3,subQ2,subQ1,subQ0]),TDD([subQ4])]})],"blendedInto":[makeQuery(id+"F11.opExtrude","SWEPT_FACE",FACE,{"disambiguationData":[OSD([subQ3,subQ2,subQ1,subQ0]),TDD([subQ4])]})]})])],"isStart":false});}
            chamfer(context, id + "F17", {"entities" : qUnion([Q0, Q1, Q2, Q3, Q4, Q5, Q6, Q7, Q8, Q9, Q10, Q11]), "width" : 5.08 * mm, "tangentPropagation" : true});
        }
        {
            var Q0;
            Q0=makeQuery(id+"F17.opChamfer","BLEND_FACE",FACE,{"disambiguationData":[OSD([sQuery(id+"F2.wireOp",EDGE,"E9")])]});
            var Q1;
            {var subQ0=sQuery(id+"F2.wireOp",EDGE,"E10");var subQ1=sQuery(id+"F2.wireOp",EDGE,"E9");var subQ2=sQuery(id+"F2.wireOp",EDGE,"E8");var subQ3=sQuery(id+"F2.wireOp",EDGE,"E7");var subQ4=makeQuery(id+"F8.opChamfer","BLEND_EDGE",EDGE,{"blendedFrom":[makeQuery(id+"F5.opExtrude","CAP_EDGE",EDGE,{"disambiguationData":[OSD([subQ1])],"isStart":false}),makeQuery(id+"F5.opExtrude","CAP_FACE",FACE,{"disambiguationData":[OSD([subQ3,subQ2,subQ1,subQ0])],"isStart":false})],"blendedInto":[makeQuery(id+"F5.opExtrude","CAP_FACE",FACE,{"disambiguationData":[OSD([subQ3,subQ2,subQ1,subQ0])],"isStart":false})]});Q1=makeQuery(id+"F17.opChamfer","BLEND_FACE",FACE,{"disambiguationData":[OSD([subQ3,subQ2,subQ1,subQ0]),TDD([makeQuery(id+"F14.opExtrude","CAP_EDGE",EDGE,{"disambiguationData":[OSD([subQ3,subQ2,subQ1,subQ0]),TDD([makeQuery(id+"F10.opChamfer","BLEND_EDGE",EDGE,{"blendedFrom":[makeQuery(id+"F9.opExtrude","CAP_EDGE",EDGE,{"disambiguationData":[OSD([subQ3,subQ2,subQ1,subQ0]),TDD([subQ4])],"isStart":false}),makeQuery(id+"F9.opExtrude","SWEPT_FACE",FACE,{"disambiguationData":[OSD([subQ3,subQ2,subQ1,subQ0]),TDD([subQ4])]})],"blendedInto":[makeQuery(id+"F9.opExtrude","SWEPT_FACE",FACE,{"disambiguationData":[OSD([subQ3,subQ2,subQ1,subQ0]),TDD([subQ4])]})]})])],"isStart":false})])]});}
            var Q2;
            {var subQ0=sQuery(id+"F2.wireOp",EDGE,"E10");var subQ1=sQuery(id+"F2.wireOp",EDGE,"E9");var subQ2=sQuery(id+"F2.wireOp",EDGE,"E8");var subQ3=sQuery(id+"F2.wireOp",EDGE,"E7");var subQ4=makeQuery(id+"F10.opChamfer","BLEND_EDGE",EDGE,{"blendedFrom":[makeQuery(id+"F9.opExtrude","CAP_EDGE",EDGE,{"disambiguationData":[OSD([subQ3,subQ2,subQ1,subQ0]),TDD([makeQuery(id+"F8.opChamfer","BLEND_EDGE",EDGE,{"blendedFrom":[makeQuery(id+"F5.opExtrude","CAP_EDGE",EDGE,{"disambiguationData":[OSD([subQ1])],"isStart":false}),makeQuery(id+"F5.opExtrude","CAP_FACE",FACE,{"disambiguationData":[OSD([subQ3,subQ2,subQ1,subQ0])],"isStart":false})],"blendedInto":[makeQuery(id+"F5.opExtrude","CAP_FACE",FACE,{"disambiguationData":[OSD([subQ3,subQ2,subQ1,subQ0])],"isStart":false})]})])],"isStart":false}),makeQuery(id+"F9.opExtrude","CAP_FACE",FACE,{"disambiguationData":[OSD([subQ3,subQ2,subQ1,subQ0])],"isStart":false})],"blendedInto":[makeQuery(id+"F9.opExtrude","CAP_FACE",FACE,{"disambiguationData":[OSD([subQ3,subQ2,subQ1,subQ0])],"isStart":false})]});Q2=makeQuery(id+"F17.opChamfer","BLEND_FACE",FACE,{"disambiguationData":[OSD([subQ3,subQ2,subQ1,subQ0]),TDD([makeQuery(id+"F14.opExtrude","CAP_EDGE",EDGE,{"disambiguationData":[OSD([subQ3,subQ2,subQ1,subQ0]),TDD([makeQuery(id+"F12.opChamfer","BLEND_EDGE",EDGE,{"blendedFrom":[makeQuery(id+"F11.opExtrude","CAP_EDGE",EDGE,{"disambiguationData":[OSD([subQ3,subQ2,subQ1,subQ0]),TDD([subQ4])],"isStart":false}),makeQuery(id+"F11.opExtrude","SWEPT_FACE",FACE,{"disambiguationData":[OSD([subQ3,subQ2,subQ1,subQ0]),TDD([subQ4])]})],"blendedInto":[makeQuery(id+"F11.opExtrude","SWEPT_FACE",FACE,{"disambiguationData":[OSD([subQ3,subQ2,subQ1,subQ0]),TDD([subQ4])]})]})])],"isStart":false})])]});}
            extrude(context, id + "F18", {"entities" : qUnion([Q0, Q1, Q2]), "operationType" : NewBodyOperationType.ADD, "depth" : 25.4 * mm});
        }
        {
            var Q0;
            Q0=makeQuery(id+"F17.opChamfer","BLEND_FACE",FACE,{"disambiguationData":[OSD([sQuery(id+"F2.wireOp",EDGE,"E10")])]});
            var Q1;
            {var subQ0=sQuery(id+"F2.wireOp",EDGE,"E10");var subQ1=sQuery(id+"F2.wireOp",EDGE,"E9");var subQ2=sQuery(id+"F2.wireOp",EDGE,"E8");var subQ3=sQuery(id+"F2.wireOp",EDGE,"E7");var subQ4=makeQuery(id+"F8.opChamfer","BLEND_EDGE",EDGE,{"blendedFrom":[makeQuery(id+"F5.opExtrude","CAP_EDGE",EDGE,{"disambiguationData":[OSD([subQ0])],"isStart":false}),makeQuery(id+"F5.opExtrude","CAP_FACE",FACE,{"disambiguationData":[OSD([subQ3,subQ2,subQ1,subQ0])],"isStart":false})],"blendedInto":[makeQuery(id+"F5.opExtrude","CAP_FACE",FACE,{"disambiguationData":[OSD([subQ3,subQ2,subQ1,subQ0])],"isStart":false})]});Q1=makeQuery(id+"F17.opChamfer","BLEND_FACE",FACE,{"disambiguationData":[OSD([subQ3,subQ2,subQ1,subQ0]),TDD([makeQuery(id+"F13.opExtrude","CAP_EDGE",EDGE,{"disambiguationData":[OSD([subQ3,subQ2,subQ1,subQ0]),TDD([makeQuery(id+"F10.opChamfer","BLEND_EDGE",EDGE,{"blendedFrom":[makeQuery(id+"F9.opExtrude","CAP_EDGE",EDGE,{"disambiguationData":[OSD([subQ3,subQ2,subQ1,subQ0]),TDD([subQ4])],"isStart":false}),makeQuery(id+"F9.opExtrude","SWEPT_FACE",FACE,{"disambiguationData":[OSD([subQ3,subQ2,subQ1,subQ0]),TDD([subQ4])]})],"blendedInto":[makeQuery(id+"F9.opExtrude","SWEPT_FACE",FACE,{"disambiguationData":[OSD([subQ3,subQ2,subQ1,subQ0]),TDD([subQ4])]})]})])],"isStart":false})])]});}
            var Q2;
            {var subQ0=sQuery(id+"F2.wireOp",EDGE,"E10");var subQ1=sQuery(id+"F2.wireOp",EDGE,"E9");var subQ2=sQuery(id+"F2.wireOp",EDGE,"E8");var subQ3=sQuery(id+"F2.wireOp",EDGE,"E7");var subQ4=makeQuery(id+"F10.opChamfer","BLEND_EDGE",EDGE,{"blendedFrom":[makeQuery(id+"F9.opExtrude","CAP_EDGE",EDGE,{"disambiguationData":[OSD([subQ3,subQ2,subQ1,subQ0]),TDD([makeQuery(id+"F8.opChamfer","BLEND_EDGE",EDGE,{"blendedFrom":[makeQuery(id+"F5.opExtrude","CAP_EDGE",EDGE,{"disambiguationData":[OSD([subQ0])],"isStart":false}),makeQuery(id+"F5.opExtrude","CAP_FACE",FACE,{"disambiguationData":[OSD([subQ3,subQ2,subQ1,subQ0])],"isStart":false})],"blendedInto":[makeQuery(id+"F5.opExtrude","CAP_FACE",FACE,{"disambiguationData":[OSD([subQ3,subQ2,subQ1,subQ0])],"isStart":false})]})])],"isStart":false}),makeQuery(id+"F9.opExtrude","CAP_FACE",FACE,{"disambiguationData":[OSD([subQ3,subQ2,subQ1,subQ0])],"isStart":false})],"blendedInto":[makeQuery(id+"F9.opExtrude","CAP_FACE",FACE,{"disambiguationData":[OSD([subQ3,subQ2,subQ1,subQ0])],"isStart":false})]});Q2=makeQuery(id+"F17.opChamfer","BLEND_FACE",FACE,{"disambiguationData":[OSD([subQ3,subQ2,subQ1,subQ0]),TDD([makeQuery(id+"F13.opExtrude","CAP_EDGE",EDGE,{"disambiguationData":[OSD([subQ3,subQ2,subQ1,subQ0]),TDD([makeQuery(id+"F12.opChamfer","BLEND_EDGE",EDGE,{"blendedFrom":[makeQuery(id+"F11.opExtrude","CAP_EDGE",EDGE,{"disambiguationData":[OSD([subQ3,subQ2,subQ1,subQ0]),TDD([subQ4])],"isStart":false}),makeQuery(id+"F11.opExtrude","SWEPT_FACE",FACE,{"disambiguationData":[OSD([subQ3,subQ2,subQ1,subQ0]),TDD([subQ4])]})],"blendedInto":[makeQuery(id+"F11.opExtrude","SWEPT_FACE",FACE,{"disambiguationData":[OSD([subQ3,subQ2,subQ1,subQ0]),TDD([subQ4])]})]})])],"isStart":false})])]});}
            extrude(context, id + "F19", {"entities" : qUnion([Q0, Q1, Q2]), "operationType" : NewBodyOperationType.ADD, "depth" : 25.4 * mm});
        }
        {
            var Q0;
            {var subQ0=sQuery(id+"F2.wireOp",EDGE,"E10");var subQ1=sQuery(id+"F2.wireOp",EDGE,"E9");var subQ2=sQuery(id+"F2.wireOp",EDGE,"E8");var subQ3=sQuery(id+"F2.wireOp",EDGE,"E7");var subQ4=makeQuery(id+"F10.opChamfer","BLEND_EDGE",EDGE,{"blendedFrom":[makeQuery(id+"F9.opExtrude","CAP_EDGE",EDGE,{"disambiguationData":[OSD([subQ3,subQ2,subQ1,subQ0]),TDD([makeQuery(id+"F8.opChamfer","BLEND_EDGE",EDGE,{"blendedFrom":[makeQuery(id+"F5.opExtrude","CAP_EDGE",EDGE,{"disambiguationData":[OSD([subQ3])],"isStart":false}),makeQuery(id+"F5.opExtrude","CAP_FACE",FACE,{"disambiguationData":[OSD([subQ3,subQ2,subQ1,subQ0])],"isStart":false})],"blendedInto":[makeQuery(id+"F5.opExtrude","CAP_FACE",FACE,{"disambiguationData":[OSD([subQ3,subQ2,subQ1,subQ0])],"isStart":false})]})])],"isStart":false}),makeQuery(id+"F9.opExtrude","CAP_FACE",FACE,{"disambiguationData":[OSD([subQ3,subQ2,subQ1,subQ0])],"isStart":false})],"blendedInto":[makeQuery(id+"F9.opExtrude","CAP_FACE",FACE,{"disambiguationData":[OSD([subQ3,subQ2,subQ1,subQ0])],"isStart":false})]});Q0=makeQuery(id+"F17.opChamfer","BLEND_FACE",FACE,{"disambiguationData":[OSD([subQ3,subQ2,subQ1,subQ0]),TDD([makeQuery(id+"F15.opExtrude","CAP_EDGE",EDGE,{"disambiguationData":[OSD([subQ3,subQ2,subQ1,subQ0]),TDD([makeQuery(id+"F12.opChamfer","BLEND_EDGE",EDGE,{"blendedFrom":[makeQuery(id+"F11.opExtrude","CAP_EDGE",EDGE,{"disambiguationData":[OSD([subQ3,subQ2,subQ1,subQ0]),TDD([subQ4])],"isStart":false}),makeQuery(id+"F11.opExtrude","SWEPT_FACE",FACE,{"disambiguationData":[OSD([subQ3,subQ2,subQ1,subQ0]),TDD([subQ4])]})],"blendedInto":[makeQuery(id+"F11.opExtrude","SWEPT_FACE",FACE,{"disambiguationData":[OSD([subQ3,subQ2,subQ1,subQ0]),TDD([subQ4])]})]})])],"isStart":false})])]});}
            var Q1;
            {var subQ0=sQuery(id+"F2.wireOp",EDGE,"E10");var subQ1=sQuery(id+"F2.wireOp",EDGE,"E9");var subQ2=sQuery(id+"F2.wireOp",EDGE,"E8");var subQ3=sQuery(id+"F2.wireOp",EDGE,"E7");var subQ4=makeQuery(id+"F8.opChamfer","BLEND_EDGE",EDGE,{"blendedFrom":[makeQuery(id+"F5.opExtrude","CAP_EDGE",EDGE,{"disambiguationData":[OSD([subQ3])],"isStart":false}),makeQuery(id+"F5.opExtrude","CAP_FACE",FACE,{"disambiguationData":[OSD([subQ3,subQ2,subQ1,subQ0])],"isStart":false})],"blendedInto":[makeQuery(id+"F5.opExtrude","CAP_FACE",FACE,{"disambiguationData":[OSD([subQ3,subQ2,subQ1,subQ0])],"isStart":false})]});Q1=makeQuery(id+"F17.opChamfer","BLEND_FACE",FACE,{"disambiguationData":[OSD([subQ3,subQ2,subQ1,subQ0]),TDD([makeQuery(id+"F15.opExtrude","CAP_EDGE",EDGE,{"disambiguationData":[OSD([subQ3,subQ2,subQ1,subQ0]),TDD([makeQuery(id+"F10.opChamfer","BLEND_EDGE",EDGE,{"blendedFrom":[makeQuery(id+"F9.opExtrude","CAP_EDGE",EDGE,{"disambiguationData":[OSD([subQ3,subQ2,subQ1,subQ0]),TDD([subQ4])],"isStart":false}),makeQuery(id+"F9.opExtrude","SWEPT_FACE",FACE,{"disambiguationData":[OSD([subQ3,subQ2,subQ1,subQ0]),TDD([subQ4])]})],"blendedInto":[makeQuery(id+"F9.opExtrude","SWEPT_FACE",FACE,{"disambiguationData":[OSD([subQ3,subQ2,subQ1,subQ0]),TDD([subQ4])]})]})])],"isStart":false})])]});}
            var Q2;
            Q2=makeQuery(id+"F17.opChamfer","BLEND_FACE",FACE,{"disambiguationData":[OSD([sQuery(id+"F2.wireOp",EDGE,"E7")])]});
            extrude(context, id + "F20", {"entities" : qUnion([Q0, Q1, Q2]), "operationType" : NewBodyOperationType.ADD, "depth" : 25.4 * mm});
        }
        {
            var Q0;
            Q0=makeQuery(id+"F17.opChamfer","BLEND_FACE",FACE,{"disambiguationData":[OSD([sQuery(id+"F2.wireOp",EDGE,"E8")])]});
            var Q1;
            {var subQ0=sQuery(id+"F2.wireOp",EDGE,"E10");var subQ1=sQuery(id+"F2.wireOp",EDGE,"E9");var subQ2=sQuery(id+"F2.wireOp",EDGE,"E8");var subQ3=sQuery(id+"F2.wireOp",EDGE,"E7");var subQ4=makeQuery(id+"F8.opChamfer","BLEND_EDGE",EDGE,{"blendedFrom":[makeQuery(id+"F5.opExtrude","CAP_EDGE",EDGE,{"disambiguationData":[OSD([subQ2])],"isStart":false}),makeQuery(id+"F5.opExtrude","CAP_FACE",FACE,{"disambiguationData":[OSD([subQ3,subQ2,subQ1,subQ0])],"isStart":false})],"blendedInto":[makeQuery(id+"F5.opExtrude","CAP_FACE",FACE,{"disambiguationData":[OSD([subQ3,subQ2,subQ1,subQ0])],"isStart":false})]});Q1=makeQuery(id+"F17.opChamfer","BLEND_FACE",FACE,{"disambiguationData":[OSD([subQ3,subQ2,subQ1,subQ0]),TDD([makeQuery(id+"F16.opExtrude","CAP_EDGE",EDGE,{"disambiguationData":[OSD([subQ3,subQ2,subQ1,subQ0]),TDD([makeQuery(id+"F10.opChamfer","BLEND_EDGE",EDGE,{"blendedFrom":[makeQuery(id+"F9.opExtrude","CAP_EDGE",EDGE,{"disambiguationData":[OSD([subQ3,subQ2,subQ1,subQ0]),TDD([subQ4])],"isStart":false}),makeQuery(id+"F9.opExtrude","SWEPT_FACE",FACE,{"disambiguationData":[OSD([subQ3,subQ2,subQ1,subQ0]),TDD([subQ4])]})],"blendedInto":[makeQuery(id+"F9.opExtrude","SWEPT_FACE",FACE,{"disambiguationData":[OSD([subQ3,subQ2,subQ1,subQ0]),TDD([subQ4])]})]})])],"isStart":false})])]});}
            var Q2;
            {var subQ0=sQuery(id+"F2.wireOp",EDGE,"E10");var subQ1=sQuery(id+"F2.wireOp",EDGE,"E9");var subQ2=sQuery(id+"F2.wireOp",EDGE,"E8");var subQ3=sQuery(id+"F2.wireOp",EDGE,"E7");var subQ4=makeQuery(id+"F10.opChamfer","BLEND_EDGE",EDGE,{"blendedFrom":[makeQuery(id+"F9.opExtrude","CAP_EDGE",EDGE,{"disambiguationData":[OSD([subQ3,subQ2,subQ1,subQ0]),TDD([makeQuery(id+"F8.opChamfer","BLEND_EDGE",EDGE,{"blendedFrom":[makeQuery(id+"F5.opExtrude","CAP_EDGE",EDGE,{"disambiguationData":[OSD([subQ2])],"isStart":false}),makeQuery(id+"F5.opExtrude","CAP_FACE",FACE,{"disambiguationData":[OSD([subQ3,subQ2,subQ1,subQ0])],"isStart":false})],"blendedInto":[makeQuery(id+"F5.opExtrude","CAP_FACE",FACE,{"disambiguationData":[OSD([subQ3,subQ2,subQ1,subQ0])],"isStart":false})]})])],"isStart":false}),makeQuery(id+"F9.opExtrude","CAP_FACE",FACE,{"disambiguationData":[OSD([subQ3,subQ2,subQ1,subQ0])],"isStart":false})],"blendedInto":[makeQuery(id+"F9.opExtrude","CAP_FACE",FACE,{"disambiguationData":[OSD([subQ3,subQ2,subQ1,subQ0])],"isStart":false})]});Q2=makeQuery(id+"F17.opChamfer","BLEND_FACE",FACE,{"disambiguationData":[OSD([subQ3,subQ2,subQ1,subQ0]),TDD([makeQuery(id+"F16.opExtrude","CAP_EDGE",EDGE,{"disambiguationData":[OSD([subQ3,subQ2,subQ1,subQ0]),TDD([makeQuery(id+"F12.opChamfer","BLEND_EDGE",EDGE,{"blendedFrom":[makeQuery(id+"F11.opExtrude","CAP_EDGE",EDGE,{"disambiguationData":[OSD([subQ3,subQ2,subQ1,subQ0]),TDD([subQ4])],"isStart":false}),makeQuery(id+"F11.opExtrude","SWEPT_FACE",FACE,{"disambiguationData":[OSD([subQ3,subQ2,subQ1,subQ0]),TDD([subQ4])]})],"blendedInto":[makeQuery(id+"F11.opExtrude","SWEPT_FACE",FACE,{"disambiguationData":[OSD([subQ3,subQ2,subQ1,subQ0]),TDD([subQ4])]})]})])],"isStart":false})])]});}
            extrude(context, id + "F21", {"entities" : qUnion([Q0, Q1, Q2]), "operationType" : NewBodyOperationType.ADD, "depth" : 25.4 * mm});
        }
        {
            var Q0;
            {var subQ0=sQuery(id+"F2.wireOp",EDGE,"E10");var subQ1=sQuery(id+"F2.wireOp",EDGE,"E9");var subQ2=sQuery(id+"F2.wireOp",EDGE,"E8");var subQ3=sQuery(id+"F2.wireOp",EDGE,"E7");var subQ4=makeQuery(id+"F9.opExtrude","CAP_FACE",FACE,{"disambiguationData":[OSD([subQ3,subQ2,subQ1,subQ0])],"isStart":false});var subQ5=makeQuery(id+"F5.opExtrude","CAP_FACE",FACE,{"disambiguationData":[OSD([subQ3,subQ2,subQ1,subQ0])],"isStart":false});var subQ6=makeQuery(id+"F10.opChamfer","BLEND_EDGE",EDGE,{"blendedFrom":[makeQuery(id+"F9.opExtrude","CAP_EDGE",EDGE,{"disambiguationData":[OSD([subQ3,subQ2,subQ1,subQ0]),TDD([makeQuery(id+"F8.opChamfer","BLEND_EDGE",EDGE,{"blendedFrom":[makeQuery(id+"F5.opExtrude","CAP_EDGE",EDGE,{"disambiguationData":[OSD([subQ1])],"isStart":false}),subQ5],"blendedInto":[subQ5]})])],"isStart":false}),subQ4],"blendedInto":[subQ4]});var subQ7=makeQuery(id+"F11.opExtrude","CAP_EDGE",EDGE,{"disambiguationData":[OSD([subQ3,subQ2,subQ1,subQ0]),TDD([subQ6])],"isStart":false});Q0=makeQuery(id+"F18.opExtrude","SWEPT_FACE",FACE,{"disambiguationData":[OSD([subQ3,subQ2,subQ1,subQ0]),TDD([makeQuery(id+"F17.opChamfer","BLEND_EDGE",EDGE,{"blendedFrom":[makeQuery(id+"F14.opExtrude","CAP_EDGE",EDGE,{"disambiguationData":[OSD([subQ3,subQ2,subQ1,subQ0]),TDD([makeQuery(id+"F12.opChamfer","BLEND_EDGE",EDGE,{"blendedFrom":[subQ7,makeQuery(id+"F11.opExtrude","SWEPT_FACE",FACE,{"disambiguationData":[OSD([subQ3,subQ2,subQ1,subQ0]),TDD([subQ6])]})],"blendedInto":[makeQuery(id+"F11.opExtrude","SWEPT_FACE",FACE,{"disambiguationData":[OSD([subQ3,subQ2,subQ1,subQ0]),TDD([subQ6])]})]})])],"isStart":false}),makeQuery(id+"F14.opExtrude","SWEPT_FACE",FACE,{"disambiguationData":[OSD([subQ3,subQ2,subQ1,subQ0]),TDD([makeQuery(id+"F12.opChamfer","BLEND_EDGE",EDGE,{"blendedFrom":[makeQuery(id+"F11.opExtrude","CAP_EDGE",EDGE,{"disambiguationData":[OSD([subQ3,subQ2,subQ1,subQ0]),TDD([makeQuery(id+"F10.opChamfer","BLEND_EDGE",EDGE,{"blendedFrom":[makeQuery(id+"F9.opExtrude","CAP_EDGE",EDGE,{"disambiguationData":[OSD([subQ3,subQ2,subQ1,subQ0]),TDD([makeQuery(id+"F8.opChamfer","BLEND_EDGE",EDGE,{"blendedFrom":[makeQuery(id+"F5.opExtrude","CAP_EDGE",EDGE,{"disambiguationData":[OSD([subQ2])],"isStart":false}),subQ5],"blendedInto":[subQ5]})])],"isStart":false}),subQ4],"blendedInto":[subQ4]})])],"isStart":false}),subQ7],"blendedInto":[]})])]})],"blendedInto":[makeQuery(id+"F14.opExtrude","SWEPT_FACE",FACE,{"disambiguationData":[OSD([subQ3,subQ2,subQ1,subQ0]),TDD([makeQuery(id+"F12.opChamfer","BLEND_EDGE",EDGE,{"blendedFrom":[makeQuery(id+"F11.opExtrude","CAP_EDGE",EDGE,{"disambiguationData":[OSD([subQ3,subQ2,subQ1,subQ0]),TDD([makeQuery(id+"F10.opChamfer","BLEND_EDGE",EDGE,{"blendedFrom":[makeQuery(id+"F9.opExtrude","CAP_EDGE",EDGE,{"disambiguationData":[OSD([subQ3,subQ2,subQ1,subQ0]),TDD([makeQuery(id+"F8.opChamfer","BLEND_EDGE",EDGE,{"blendedFrom":[makeQuery(id+"F5.opExtrude","CAP_EDGE",EDGE,{"disambiguationData":[OSD([subQ2])],"isStart":false}),subQ5],"blendedInto":[subQ5]})])],"isStart":false}),subQ4],"blendedInto":[subQ4]})])],"isStart":false}),subQ7],"blendedInto":[]})])]})]})])]});}
            var Q1;
            {var subQ0=sQuery(id+"F2.wireOp",EDGE,"E10");var subQ1=sQuery(id+"F2.wireOp",EDGE,"E9");var subQ2=sQuery(id+"F2.wireOp",EDGE,"E8");var subQ3=sQuery(id+"F2.wireOp",EDGE,"E7");var subQ4=makeQuery(id+"F5.opExtrude","CAP_FACE",FACE,{"disambiguationData":[OSD([subQ3,subQ2,subQ1,subQ0])],"isStart":false});var subQ5=makeQuery(id+"F8.opChamfer","BLEND_EDGE",EDGE,{"blendedFrom":[makeQuery(id+"F5.opExtrude","CAP_EDGE",EDGE,{"disambiguationData":[OSD([subQ1])],"isStart":false}),subQ4],"blendedInto":[subQ4]});var subQ6=makeQuery(id+"F9.opExtrude","CAP_EDGE",EDGE,{"disambiguationData":[OSD([subQ3,subQ2,subQ1,subQ0]),TDD([subQ5])],"isStart":false});Q1=makeQuery(id+"F18.opExtrude","SWEPT_FACE",FACE,{"disambiguationData":[OSD([subQ3,subQ2,subQ1,subQ0]),TDD([makeQuery(id+"F17.opChamfer","BLEND_EDGE",EDGE,{"blendedFrom":[makeQuery(id+"F14.opExtrude","CAP_EDGE",EDGE,{"disambiguationData":[OSD([subQ3,subQ2,subQ1,subQ0]),TDD([makeQuery(id+"F10.opChamfer","BLEND_EDGE",EDGE,{"blendedFrom":[subQ6,makeQuery(id+"F9.opExtrude","SWEPT_FACE",FACE,{"disambiguationData":[OSD([subQ3,subQ2,subQ1,subQ0]),TDD([subQ5])]})],"blendedInto":[makeQuery(id+"F9.opExtrude","SWEPT_FACE",FACE,{"disambiguationData":[OSD([subQ3,subQ2,subQ1,subQ0]),TDD([subQ5])]})]})])],"isStart":false}),makeQuery(id+"F14.opExtrude","SWEPT_FACE",FACE,{"disambiguationData":[OSD([subQ3,subQ2,subQ1,subQ0]),TDD([makeQuery(id+"F10.opChamfer","BLEND_EDGE",EDGE,{"blendedFrom":[makeQuery(id+"F9.opExtrude","CAP_EDGE",EDGE,{"disambiguationData":[OSD([subQ3,subQ2,subQ1,subQ0]),TDD([makeQuery(id+"F8.opChamfer","BLEND_EDGE",EDGE,{"blendedFrom":[makeQuery(id+"F5.opExtrude","CAP_EDGE",EDGE,{"disambiguationData":[OSD([subQ2])],"isStart":false}),subQ4],"blendedInto":[subQ4]})])],"isStart":false}),subQ6],"blendedInto":[]})])]})],"blendedInto":[makeQuery(id+"F14.opExtrude","SWEPT_FACE",FACE,{"disambiguationData":[OSD([subQ3,subQ2,subQ1,subQ0]),TDD([makeQuery(id+"F10.opChamfer","BLEND_EDGE",EDGE,{"blendedFrom":[makeQuery(id+"F9.opExtrude","CAP_EDGE",EDGE,{"disambiguationData":[OSD([subQ3,subQ2,subQ1,subQ0]),TDD([makeQuery(id+"F8.opChamfer","BLEND_EDGE",EDGE,{"blendedFrom":[makeQuery(id+"F5.opExtrude","CAP_EDGE",EDGE,{"disambiguationData":[OSD([subQ2])],"isStart":false}),subQ4],"blendedInto":[subQ4]})])],"isStart":false}),subQ6],"blendedInto":[]})])]})]})])]});}
            var Q2;
            Q2=makeQuery(id+"F18.opExtrude","SWEPT_FACE",FACE,{"disambiguationData":[OSD([sQuery(id+"F2.wireOp",EDGE,"E8"),sQuery(id+"F2.wireOp",EDGE,"E9")])]});
            extrude(context, id + "F22", {"entities" : qUnion([Q0, Q1, Q2]), "operationType" : NewBodyOperationType.ADD, "depth" : 25.4 * mm});
        }
        {
            var Q0;
            {var subQ0=sQuery(id+"F2.wireOp",EDGE,"E10");var subQ1=sQuery(id+"F2.wireOp",EDGE,"E9");var subQ2=sQuery(id+"F2.wireOp",EDGE,"E8");var subQ3=sQuery(id+"F2.wireOp",EDGE,"E7");var subQ4=makeQuery(id+"F9.opExtrude","CAP_FACE",FACE,{"disambiguationData":[OSD([subQ3,subQ2,subQ1,subQ0])],"isStart":false});var subQ5=makeQuery(id+"F5.opExtrude","CAP_FACE",FACE,{"disambiguationData":[OSD([subQ3,subQ2,subQ1,subQ0])],"isStart":false});var subQ6=makeQuery(id+"F10.opChamfer","BLEND_EDGE",EDGE,{"blendedFrom":[makeQuery(id+"F9.opExtrude","CAP_EDGE",EDGE,{"disambiguationData":[OSD([subQ3,subQ2,subQ1,subQ0]),TDD([makeQuery(id+"F8.opChamfer","BLEND_EDGE",EDGE,{"blendedFrom":[makeQuery(id+"F5.opExtrude","CAP_EDGE",EDGE,{"disambiguationData":[OSD([subQ2])],"isStart":false}),subQ5],"blendedInto":[subQ5]})])],"isStart":false}),subQ4],"blendedInto":[subQ4]});var subQ7=makeQuery(id+"F11.opExtrude","CAP_EDGE",EDGE,{"disambiguationData":[OSD([subQ3,subQ2,subQ1,subQ0]),TDD([subQ6])],"isStart":false});var subQ8=makeQuery(id+"F12.opChamfer","BLEND_EDGE",EDGE,{"blendedFrom":[subQ7,makeQuery(id+"F11.opExtrude","CAP_EDGE",EDGE,{"disambiguationData":[OSD([subQ3,subQ2,subQ1,subQ0]),TDD([makeQuery(id+"F10.opChamfer","BLEND_EDGE",EDGE,{"blendedFrom":[makeQuery(id+"F9.opExtrude","CAP_EDGE",EDGE,{"disambiguationData":[OSD([subQ3,subQ2,subQ1,subQ0]),TDD([makeQuery(id+"F8.opChamfer","BLEND_EDGE",EDGE,{"blendedFrom":[makeQuery(id+"F5.opExtrude","CAP_EDGE",EDGE,{"disambiguationData":[OSD([subQ1])],"isStart":false}),subQ5],"blendedInto":[subQ5]})])],"isStart":false}),subQ4],"blendedInto":[subQ4]})])],"isStart":false})],"blendedInto":[]});Q0=makeQuery(id+"F21.opExtrude","SWEPT_FACE",FACE,{"disambiguationData":[OSD([subQ3,subQ2,subQ1,subQ0]),TDD([makeQuery(id+"F17.opChamfer","BLEND_EDGE",EDGE,{"blendedFrom":[makeQuery(id+"F16.opExtrude","CAP_EDGE",EDGE,{"disambiguationData":[OSD([subQ3,subQ2,subQ1,subQ0]),TDD([makeQuery(id+"F12.opChamfer","BLEND_EDGE",EDGE,{"blendedFrom":[subQ7,makeQuery(id+"F11.opExtrude","SWEPT_FACE",FACE,{"disambiguationData":[OSD([subQ3,subQ2,subQ1,subQ0]),TDD([subQ6])]})],"blendedInto":[makeQuery(id+"F11.opExtrude","SWEPT_FACE",FACE,{"disambiguationData":[OSD([subQ3,subQ2,subQ1,subQ0]),TDD([subQ6])]})]})])],"isStart":false}),makeQuery(id+"F16.opExtrude","SWEPT_FACE",FACE,{"disambiguationData":[OSD([subQ3,subQ2,subQ1,subQ0]),TDD([makeQuery(id+"F14.boolean.opBoolean","MERGE",EDGE,{"derivedFrom":[subQ8,makeQuery(id+"F14.opExtrude","CAP_EDGE",EDGE,{"disambiguationData":[OSD([subQ3,subQ2,subQ1,subQ0]),TDD([subQ8])],"isStart":true})]})])]})],"blendedInto":[makeQuery(id+"F16.opExtrude","SWEPT_FACE",FACE,{"disambiguationData":[OSD([subQ3,subQ2,subQ1,subQ0]),TDD([makeQuery(id+"F14.boolean.opBoolean","MERGE",EDGE,{"derivedFrom":[subQ8,makeQuery(id+"F14.opExtrude","CAP_EDGE",EDGE,{"disambiguationData":[OSD([subQ3,subQ2,subQ1,subQ0]),TDD([subQ8])],"isStart":true})]})])]})]})])]});}
            var Q1;
            {var subQ0=sQuery(id+"F2.wireOp",EDGE,"E10");var subQ1=sQuery(id+"F2.wireOp",EDGE,"E9");var subQ2=sQuery(id+"F2.wireOp",EDGE,"E8");var subQ3=sQuery(id+"F2.wireOp",EDGE,"E7");var subQ4=makeQuery(id+"F5.opExtrude","CAP_FACE",FACE,{"disambiguationData":[OSD([subQ3,subQ2,subQ1,subQ0])],"isStart":false});var subQ5=makeQuery(id+"F8.opChamfer","BLEND_EDGE",EDGE,{"blendedFrom":[makeQuery(id+"F5.opExtrude","CAP_EDGE",EDGE,{"disambiguationData":[OSD([subQ2])],"isStart":false}),subQ4],"blendedInto":[subQ4]});var subQ6=makeQuery(id+"F9.opExtrude","CAP_EDGE",EDGE,{"disambiguationData":[OSD([subQ3,subQ2,subQ1,subQ0]),TDD([subQ5])],"isStart":false});var subQ7=makeQuery(id+"F10.opChamfer","BLEND_EDGE",EDGE,{"blendedFrom":[subQ6,makeQuery(id+"F9.opExtrude","CAP_EDGE",EDGE,{"disambiguationData":[OSD([subQ3,subQ2,subQ1,subQ0]),TDD([makeQuery(id+"F8.opChamfer","BLEND_EDGE",EDGE,{"blendedFrom":[makeQuery(id+"F5.opExtrude","CAP_EDGE",EDGE,{"disambiguationData":[OSD([subQ1])],"isStart":false}),subQ4],"blendedInto":[subQ4]})])],"isStart":false})],"blendedInto":[]});Q1=makeQuery(id+"F21.opExtrude","SWEPT_FACE",FACE,{"disambiguationData":[OSD([subQ3,subQ2,subQ1,subQ0]),TDD([makeQuery(id+"F17.opChamfer","BLEND_EDGE",EDGE,{"blendedFrom":[makeQuery(id+"F16.opExtrude","CAP_EDGE",EDGE,{"disambiguationData":[OSD([subQ3,subQ2,subQ1,subQ0]),TDD([makeQuery(id+"F10.opChamfer","BLEND_EDGE",EDGE,{"blendedFrom":[subQ6,makeQuery(id+"F9.opExtrude","SWEPT_FACE",FACE,{"disambiguationData":[OSD([subQ3,subQ2,subQ1,subQ0]),TDD([subQ5])]})],"blendedInto":[makeQuery(id+"F9.opExtrude","SWEPT_FACE",FACE,{"disambiguationData":[OSD([subQ3,subQ2,subQ1,subQ0]),TDD([subQ5])]})]})])],"isStart":false}),makeQuery(id+"F16.opExtrude","SWEPT_FACE",FACE,{"disambiguationData":[OSD([subQ3,subQ2,subQ1,subQ0]),TDD([makeQuery(id+"F14.boolean.opBoolean","MERGE",EDGE,{"derivedFrom":[subQ7,makeQuery(id+"F14.opExtrude","CAP_EDGE",EDGE,{"disambiguationData":[OSD([subQ3,subQ2,subQ1,subQ0]),TDD([subQ7])],"isStart":true})]})])]})],"blendedInto":[makeQuery(id+"F16.opExtrude","SWEPT_FACE",FACE,{"disambiguationData":[OSD([subQ3,subQ2,subQ1,subQ0]),TDD([makeQuery(id+"F14.boolean.opBoolean","MERGE",EDGE,{"derivedFrom":[subQ7,makeQuery(id+"F14.opExtrude","CAP_EDGE",EDGE,{"disambiguationData":[OSD([subQ3,subQ2,subQ1,subQ0]),TDD([subQ7])],"isStart":true})]})])]})]})])]});}
            var Q2;
            Q2=makeQuery(id+"F21.opExtrude","SWEPT_FACE",FACE,{"disambiguationData":[OSD([sQuery(id+"F2.wireOp",EDGE,"E8"),sQuery(id+"F2.wireOp",EDGE,"E9")])]});
            extrude(context, id + "F23", {"entities" : qUnion([Q0, Q1, Q2]), "operationType" : NewBodyOperationType.ADD, "depth" : 25.4 * mm});
        }
        {
            var Q0;
            Q0=makeQuery(id+"F20.opExtrude","SWEPT_FACE",FACE,{"disambiguationData":[OSD([sQuery(id+"F2.wireOp",EDGE,"E7"),sQuery(id+"F2.wireOp",EDGE,"E10")])]});
            var Q1;
            {var subQ0=sQuery(id+"F2.wireOp",EDGE,"E10");var subQ1=sQuery(id+"F2.wireOp",EDGE,"E9");var subQ2=sQuery(id+"F2.wireOp",EDGE,"E8");var subQ3=sQuery(id+"F2.wireOp",EDGE,"E7");var subQ4=makeQuery(id+"F5.opExtrude","CAP_FACE",FACE,{"disambiguationData":[OSD([subQ3,subQ2,subQ1,subQ0])],"isStart":false});var subQ5=makeQuery(id+"F8.opChamfer","BLEND_EDGE",EDGE,{"blendedFrom":[makeQuery(id+"F5.opExtrude","CAP_EDGE",EDGE,{"disambiguationData":[OSD([subQ3])],"isStart":false}),subQ4],"blendedInto":[subQ4]});var subQ6=makeQuery(id+"F9.opExtrude","CAP_EDGE",EDGE,{"disambiguationData":[OSD([subQ3,subQ2,subQ1,subQ0]),TDD([subQ5])],"isStart":false});var subQ7=makeQuery(id+"F10.opChamfer","BLEND_EDGE",EDGE,{"blendedFrom":[subQ6,makeQuery(id+"F9.opExtrude","CAP_EDGE",EDGE,{"disambiguationData":[OSD([subQ3,subQ2,subQ1,subQ0]),TDD([makeQuery(id+"F8.opChamfer","BLEND_EDGE",EDGE,{"blendedFrom":[makeQuery(id+"F5.opExtrude","CAP_EDGE",EDGE,{"disambiguationData":[OSD([subQ0])],"isStart":false}),subQ4],"blendedInto":[subQ4]})])],"isStart":false})],"blendedInto":[]});Q1=makeQuery(id+"F20.opExtrude","SWEPT_FACE",FACE,{"disambiguationData":[OSD([subQ3,subQ2,subQ1,subQ0]),TDD([makeQuery(id+"F17.opChamfer","BLEND_EDGE",EDGE,{"blendedFrom":[makeQuery(id+"F15.opExtrude","CAP_EDGE",EDGE,{"disambiguationData":[OSD([subQ3,subQ2,subQ1,subQ0]),TDD([makeQuery(id+"F10.opChamfer","BLEND_EDGE",EDGE,{"blendedFrom":[subQ6,makeQuery(id+"F9.opExtrude","SWEPT_FACE",FACE,{"disambiguationData":[OSD([subQ3,subQ2,subQ1,subQ0]),TDD([subQ5])]})],"blendedInto":[makeQuery(id+"F9.opExtrude","SWEPT_FACE",FACE,{"disambiguationData":[OSD([subQ3,subQ2,subQ1,subQ0]),TDD([subQ5])]})]})])],"isStart":false}),makeQuery(id+"F15.opExtrude","SWEPT_FACE",FACE,{"disambiguationData":[OSD([subQ3,subQ2,subQ1,subQ0]),TDD([makeQuery(id+"F13.boolean.opBoolean","MERGE",EDGE,{"derivedFrom":[subQ7,makeQuery(id+"F13.opExtrude","CAP_EDGE",EDGE,{"disambiguationData":[OSD([subQ3,subQ2,subQ1,subQ0]),TDD([subQ7])],"isStart":true})]})])]})],"blendedInto":[makeQuery(id+"F15.opExtrude","SWEPT_FACE",FACE,{"disambiguationData":[OSD([subQ3,subQ2,subQ1,subQ0]),TDD([makeQuery(id+"F13.boolean.opBoolean","MERGE",EDGE,{"derivedFrom":[subQ7,makeQuery(id+"F13.opExtrude","CAP_EDGE",EDGE,{"disambiguationData":[OSD([subQ3,subQ2,subQ1,subQ0]),TDD([subQ7])],"isStart":true})]})])]})]})])]});}
            var Q2;
            {var subQ0=sQuery(id+"F2.wireOp",EDGE,"E10");var subQ1=sQuery(id+"F2.wireOp",EDGE,"E9");var subQ2=sQuery(id+"F2.wireOp",EDGE,"E8");var subQ3=sQuery(id+"F2.wireOp",EDGE,"E7");var subQ4=makeQuery(id+"F9.opExtrude","CAP_FACE",FACE,{"disambiguationData":[OSD([subQ3,subQ2,subQ1,subQ0])],"isStart":false});var subQ5=makeQuery(id+"F5.opExtrude","CAP_FACE",FACE,{"disambiguationData":[OSD([subQ3,subQ2,subQ1,subQ0])],"isStart":false});var subQ6=makeQuery(id+"F10.opChamfer","BLEND_EDGE",EDGE,{"blendedFrom":[makeQuery(id+"F9.opExtrude","CAP_EDGE",EDGE,{"disambiguationData":[OSD([subQ3,subQ2,subQ1,subQ0]),TDD([makeQuery(id+"F8.opChamfer","BLEND_EDGE",EDGE,{"blendedFrom":[makeQuery(id+"F5.opExtrude","CAP_EDGE",EDGE,{"disambiguationData":[OSD([subQ3])],"isStart":false}),subQ5],"blendedInto":[subQ5]})])],"isStart":false}),subQ4],"blendedInto":[subQ4]});var subQ7=makeQuery(id+"F11.opExtrude","CAP_EDGE",EDGE,{"disambiguationData":[OSD([subQ3,subQ2,subQ1,subQ0]),TDD([subQ6])],"isStart":false});var subQ8=makeQuery(id+"F12.opChamfer","BLEND_EDGE",EDGE,{"blendedFrom":[subQ7,makeQuery(id+"F11.opExtrude","CAP_EDGE",EDGE,{"disambiguationData":[OSD([subQ3,subQ2,subQ1,subQ0]),TDD([makeQuery(id+"F10.opChamfer","BLEND_EDGE",EDGE,{"blendedFrom":[makeQuery(id+"F9.opExtrude","CAP_EDGE",EDGE,{"disambiguationData":[OSD([subQ3,subQ2,subQ1,subQ0]),TDD([makeQuery(id+"F8.opChamfer","BLEND_EDGE",EDGE,{"blendedFrom":[makeQuery(id+"F5.opExtrude","CAP_EDGE",EDGE,{"disambiguationData":[OSD([subQ0])],"isStart":false}),subQ5],"blendedInto":[subQ5]})])],"isStart":false}),subQ4],"blendedInto":[subQ4]})])],"isStart":false})],"blendedInto":[]});Q2=makeQuery(id+"F20.opExtrude","SWEPT_FACE",FACE,{"disambiguationData":[OSD([subQ3,subQ2,subQ1,subQ0]),TDD([makeQuery(id+"F17.opChamfer","BLEND_EDGE",EDGE,{"blendedFrom":[makeQuery(id+"F15.opExtrude","CAP_EDGE",EDGE,{"disambiguationData":[OSD([subQ3,subQ2,subQ1,subQ0]),TDD([makeQuery(id+"F12.opChamfer","BLEND_EDGE",EDGE,{"blendedFrom":[subQ7,makeQuery(id+"F11.opExtrude","SWEPT_FACE",FACE,{"disambiguationData":[OSD([subQ3,subQ2,subQ1,subQ0]),TDD([subQ6])]})],"blendedInto":[makeQuery(id+"F11.opExtrude","SWEPT_FACE",FACE,{"disambiguationData":[OSD([subQ3,subQ2,subQ1,subQ0]),TDD([subQ6])]})]})])],"isStart":false}),makeQuery(id+"F15.opExtrude","SWEPT_FACE",FACE,{"disambiguationData":[OSD([subQ3,subQ2,subQ1,subQ0]),TDD([makeQuery(id+"F13.boolean.opBoolean","MERGE",EDGE,{"derivedFrom":[subQ8,makeQuery(id+"F13.opExtrude","CAP_EDGE",EDGE,{"disambiguationData":[OSD([subQ3,subQ2,subQ1,subQ0]),TDD([subQ8])],"isStart":true})]})])]})],"blendedInto":[makeQuery(id+"F15.opExtrude","SWEPT_FACE",FACE,{"disambiguationData":[OSD([subQ3,subQ2,subQ1,subQ0]),TDD([makeQuery(id+"F13.boolean.opBoolean","MERGE",EDGE,{"derivedFrom":[subQ8,makeQuery(id+"F13.opExtrude","CAP_EDGE",EDGE,{"disambiguationData":[OSD([subQ3,subQ2,subQ1,subQ0]),TDD([subQ8])],"isStart":true})]})])]})]})])]});}
            extrude(context, id + "F24", {"entities" : qUnion([Q0, Q1, Q2]), "operationType" : NewBodyOperationType.ADD, "depth" : 25.4 * mm});
        }
        {
            var Q0;
            Q0=makeQuery(id+"F19.opExtrude","SWEPT_FACE",FACE,{"disambiguationData":[OSD([sQuery(id+"F2.wireOp",EDGE,"E7"),sQuery(id+"F2.wireOp",EDGE,"E10")])]});
            var Q1;
            {var subQ0=sQuery(id+"F2.wireOp",EDGE,"E10");var subQ1=sQuery(id+"F2.wireOp",EDGE,"E9");var subQ2=sQuery(id+"F2.wireOp",EDGE,"E8");var subQ3=sQuery(id+"F2.wireOp",EDGE,"E7");var subQ4=makeQuery(id+"F5.opExtrude","CAP_FACE",FACE,{"disambiguationData":[OSD([subQ3,subQ2,subQ1,subQ0])],"isStart":false});var subQ5=makeQuery(id+"F8.opChamfer","BLEND_EDGE",EDGE,{"blendedFrom":[makeQuery(id+"F5.opExtrude","CAP_EDGE",EDGE,{"disambiguationData":[OSD([subQ0])],"isStart":false}),subQ4],"blendedInto":[subQ4]});var subQ6=makeQuery(id+"F9.opExtrude","CAP_EDGE",EDGE,{"disambiguationData":[OSD([subQ3,subQ2,subQ1,subQ0]),TDD([subQ5])],"isStart":false});Q1=makeQuery(id+"F19.opExtrude","SWEPT_FACE",FACE,{"disambiguationData":[OSD([subQ3,subQ2,subQ1,subQ0]),TDD([makeQuery(id+"F17.opChamfer","BLEND_EDGE",EDGE,{"blendedFrom":[makeQuery(id+"F13.opExtrude","CAP_EDGE",EDGE,{"disambiguationData":[OSD([subQ3,subQ2,subQ1,subQ0]),TDD([makeQuery(id+"F10.opChamfer","BLEND_EDGE",EDGE,{"blendedFrom":[subQ6,makeQuery(id+"F9.opExtrude","SWEPT_FACE",FACE,{"disambiguationData":[OSD([subQ3,subQ2,subQ1,subQ0]),TDD([subQ5])]})],"blendedInto":[makeQuery(id+"F9.opExtrude","SWEPT_FACE",FACE,{"disambiguationData":[OSD([subQ3,subQ2,subQ1,subQ0]),TDD([subQ5])]})]})])],"isStart":false}),makeQuery(id+"F13.opExtrude","SWEPT_FACE",FACE,{"disambiguationData":[OSD([subQ3,subQ2,subQ1,subQ0]),TDD([makeQuery(id+"F10.opChamfer","BLEND_EDGE",EDGE,{"blendedFrom":[makeQuery(id+"F9.opExtrude","CAP_EDGE",EDGE,{"disambiguationData":[OSD([subQ3,subQ2,subQ1,subQ0]),TDD([makeQuery(id+"F8.opChamfer","BLEND_EDGE",EDGE,{"blendedFrom":[makeQuery(id+"F5.opExtrude","CAP_EDGE",EDGE,{"disambiguationData":[OSD([subQ3])],"isStart":false}),subQ4],"blendedInto":[subQ4]})])],"isStart":false}),subQ6],"blendedInto":[]})])]})],"blendedInto":[makeQuery(id+"F13.opExtrude","SWEPT_FACE",FACE,{"disambiguationData":[OSD([subQ3,subQ2,subQ1,subQ0]),TDD([makeQuery(id+"F10.opChamfer","BLEND_EDGE",EDGE,{"blendedFrom":[makeQuery(id+"F9.opExtrude","CAP_EDGE",EDGE,{"disambiguationData":[OSD([subQ3,subQ2,subQ1,subQ0]),TDD([makeQuery(id+"F8.opChamfer","BLEND_EDGE",EDGE,{"blendedFrom":[makeQuery(id+"F5.opExtrude","CAP_EDGE",EDGE,{"disambiguationData":[OSD([subQ3])],"isStart":false}),subQ4],"blendedInto":[subQ4]})])],"isStart":false}),subQ6],"blendedInto":[]})])]})]})])]});}
            var Q2;
            {var subQ0=sQuery(id+"F2.wireOp",EDGE,"E10");var subQ1=sQuery(id+"F2.wireOp",EDGE,"E9");var subQ2=sQuery(id+"F2.wireOp",EDGE,"E8");var subQ3=sQuery(id+"F2.wireOp",EDGE,"E7");var subQ4=makeQuery(id+"F9.opExtrude","CAP_FACE",FACE,{"disambiguationData":[OSD([subQ3,subQ2,subQ1,subQ0])],"isStart":false});var subQ5=makeQuery(id+"F5.opExtrude","CAP_FACE",FACE,{"disambiguationData":[OSD([subQ3,subQ2,subQ1,subQ0])],"isStart":false});var subQ6=makeQuery(id+"F10.opChamfer","BLEND_EDGE",EDGE,{"blendedFrom":[makeQuery(id+"F9.opExtrude","CAP_EDGE",EDGE,{"disambiguationData":[OSD([subQ3,subQ2,subQ1,subQ0]),TDD([makeQuery(id+"F8.opChamfer","BLEND_EDGE",EDGE,{"blendedFrom":[makeQuery(id+"F5.opExtrude","CAP_EDGE",EDGE,{"disambiguationData":[OSD([subQ0])],"isStart":false}),subQ5],"blendedInto":[subQ5]})])],"isStart":false}),subQ4],"blendedInto":[subQ4]});var subQ7=makeQuery(id+"F11.opExtrude","CAP_EDGE",EDGE,{"disambiguationData":[OSD([subQ3,subQ2,subQ1,subQ0]),TDD([subQ6])],"isStart":false});Q2=makeQuery(id+"F19.opExtrude","SWEPT_FACE",FACE,{"disambiguationData":[OSD([subQ3,subQ2,subQ1,subQ0]),TDD([makeQuery(id+"F17.opChamfer","BLEND_EDGE",EDGE,{"blendedFrom":[makeQuery(id+"F13.opExtrude","CAP_EDGE",EDGE,{"disambiguationData":[OSD([subQ3,subQ2,subQ1,subQ0]),TDD([makeQuery(id+"F12.opChamfer","BLEND_EDGE",EDGE,{"blendedFrom":[subQ7,makeQuery(id+"F11.opExtrude","SWEPT_FACE",FACE,{"disambiguationData":[OSD([subQ3,subQ2,subQ1,subQ0]),TDD([subQ6])]})],"blendedInto":[makeQuery(id+"F11.opExtrude","SWEPT_FACE",FACE,{"disambiguationData":[OSD([subQ3,subQ2,subQ1,subQ0]),TDD([subQ6])]})]})])],"isStart":false}),makeQuery(id+"F13.opExtrude","SWEPT_FACE",FACE,{"disambiguationData":[OSD([subQ3,subQ2,subQ1,subQ0]),TDD([makeQuery(id+"F12.opChamfer","BLEND_EDGE",EDGE,{"blendedFrom":[makeQuery(id+"F11.opExtrude","CAP_EDGE",EDGE,{"disambiguationData":[OSD([subQ3,subQ2,subQ1,subQ0]),TDD([makeQuery(id+"F10.opChamfer","BLEND_EDGE",EDGE,{"blendedFrom":[makeQuery(id+"F9.opExtrude","CAP_EDGE",EDGE,{"disambiguationData":[OSD([subQ3,subQ2,subQ1,subQ0]),TDD([makeQuery(id+"F8.opChamfer","BLEND_EDGE",EDGE,{"blendedFrom":[makeQuery(id+"F5.opExtrude","CAP_EDGE",EDGE,{"disambiguationData":[OSD([subQ3])],"isStart":false}),subQ5],"blendedInto":[subQ5]})])],"isStart":false}),subQ4],"blendedInto":[subQ4]})])],"isStart":false}),subQ7],"blendedInto":[]})])]})],"blendedInto":[makeQuery(id+"F13.opExtrude","SWEPT_FACE",FACE,{"disambiguationData":[OSD([subQ3,subQ2,subQ1,subQ0]),TDD([makeQuery(id+"F12.opChamfer","BLEND_EDGE",EDGE,{"blendedFrom":[makeQuery(id+"F11.opExtrude","CAP_EDGE",EDGE,{"disambiguationData":[OSD([subQ3,subQ2,subQ1,subQ0]),TDD([makeQuery(id+"F10.opChamfer","BLEND_EDGE",EDGE,{"blendedFrom":[makeQuery(id+"F9.opExtrude","CAP_EDGE",EDGE,{"disambiguationData":[OSD([subQ3,subQ2,subQ1,subQ0]),TDD([makeQuery(id+"F8.opChamfer","BLEND_EDGE",EDGE,{"blendedFrom":[makeQuery(id+"F5.opExtrude","CAP_EDGE",EDGE,{"disambiguationData":[OSD([subQ3])],"isStart":false}),subQ5],"blendedInto":[subQ5]})])],"isStart":false}),subQ4],"blendedInto":[subQ4]})])],"isStart":false}),subQ7],"blendedInto":[]})])]})]})])]});}
            extrude(context, id + "F25", {"entities" : qUnion([Q0, Q1, Q2]), "operationType" : NewBodyOperationType.ADD, "depth" : 25.4 * mm});
        }
        {
            var Q0;
            {var subQ0=sQuery(id+"F2.wireOp",EDGE,"E10");var subQ1=sQuery(id+"F2.wireOp",EDGE,"E9");var subQ2=sQuery(id+"F2.wireOp",EDGE,"E8");var subQ3=sQuery(id+"F2.wireOp",EDGE,"E7");var subQ4=makeQuery(id+"F9.opExtrude","CAP_FACE",FACE,{"disambiguationData":[OSD([subQ3,subQ2,subQ1,subQ0])],"isStart":false});var subQ5=makeQuery(id+"F5.opExtrude","CAP_FACE",FACE,{"disambiguationData":[OSD([subQ3,subQ2,subQ1,subQ0])],"isStart":false});var subQ6=makeQuery(id+"F10.opChamfer","BLEND_EDGE",EDGE,{"blendedFrom":[makeQuery(id+"F9.opExtrude","CAP_EDGE",EDGE,{"disambiguationData":[OSD([subQ3,subQ2,subQ1,subQ0]),TDD([makeQuery(id+"F8.opChamfer","BLEND_EDGE",EDGE,{"blendedFrom":[makeQuery(id+"F5.opExtrude","CAP_EDGE",EDGE,{"disambiguationData":[OSD([subQ1])],"isStart":false}),subQ5],"blendedInto":[subQ5]})])],"isStart":false}),subQ4],"blendedInto":[subQ4]});var subQ7=makeQuery(id+"F11.opExtrude","CAP_EDGE",EDGE,{"disambiguationData":[OSD([subQ3,subQ2,subQ1,subQ0]),TDD([subQ6])],"isStart":false});Q0=makeQuery(id+"F22.opExtrude","SWEPT_EDGE",EDGE,{"disambiguationData":[OSD([subQ3,subQ2,subQ1,subQ0]),TDD([makeQuery(id+"F18.opExtrude","CAP_VERTEX",VERTEX,{"disambiguationData":[OSD([subQ3,subQ2,subQ1,subQ0]),TDD([makeQuery(id+"F17.opChamfer","BLEND_VERTEX",VERTEX,{"blendedFrom":[makeQuery(id+"F14.opExtrude","CAP_EDGE",EDGE,{"disambiguationData":[OSD([subQ3,subQ2,subQ1,subQ0]),TDD([makeQuery(id+"F12.opChamfer","BLEND_EDGE",EDGE,{"blendedFrom":[subQ7,makeQuery(id+"F11.opExtrude","SWEPT_FACE",FACE,{"disambiguationData":[OSD([subQ3,subQ2,subQ1,subQ0]),TDD([subQ6])]})],"blendedInto":[makeQuery(id+"F11.opExtrude","SWEPT_FACE",FACE,{"disambiguationData":[OSD([subQ3,subQ2,subQ1,subQ0]),TDD([subQ6])]})]})])],"isStart":false}),makeQuery(id+"F14.opExtrude","SWEPT_FACE",FACE,{"disambiguationData":[OSD([subQ3,subQ2,subQ1,subQ0]),TDD([makeQuery(id+"F12.opChamfer","BLEND_EDGE",EDGE,{"blendedFrom":[makeQuery(id+"F11.opExtrude","CAP_EDGE",EDGE,{"disambiguationData":[OSD([subQ3,subQ2,subQ1,subQ0]),TDD([makeQuery(id+"F10.opChamfer","BLEND_EDGE",EDGE,{"blendedFrom":[makeQuery(id+"F9.opExtrude","CAP_EDGE",EDGE,{"disambiguationData":[OSD([subQ3,subQ2,subQ1,subQ0]),TDD([makeQuery(id+"F8.opChamfer","BLEND_EDGE",EDGE,{"blendedFrom":[makeQuery(id+"F5.opExtrude","CAP_EDGE",EDGE,{"disambiguationData":[OSD([subQ2])],"isStart":false}),subQ5],"blendedInto":[subQ5]})])],"isStart":false}),subQ4],"blendedInto":[subQ4]})])],"isStart":false}),subQ7],"blendedInto":[]})])]}),makeQuery(id+"F14.opExtrude","CAP_FACE",FACE,{"disambiguationData":[OSD([subQ3,subQ2,subQ1,subQ0]),TDD([makeQuery(id+"F12.opChamfer","BLEND_FACE",FACE,{"disambiguationData":[OSD([subQ3,subQ2,subQ1,subQ0]),TDD([subQ7])]})])],"isStart":false})],"blendedInto":[makeQuery(id+"F14.opExtrude","SWEPT_FACE",FACE,{"disambiguationData":[OSD([subQ3,subQ2,subQ1,subQ0]),TDD([makeQuery(id+"F12.opChamfer","BLEND_EDGE",EDGE,{"blendedFrom":[makeQuery(id+"F11.opExtrude","CAP_EDGE",EDGE,{"disambiguationData":[OSD([subQ3,subQ2,subQ1,subQ0]),TDD([makeQuery(id+"F10.opChamfer","BLEND_EDGE",EDGE,{"blendedFrom":[makeQuery(id+"F9.opExtrude","CAP_EDGE",EDGE,{"disambiguationData":[OSD([subQ3,subQ2,subQ1,subQ0]),TDD([makeQuery(id+"F8.opChamfer","BLEND_EDGE",EDGE,{"blendedFrom":[makeQuery(id+"F5.opExtrude","CAP_EDGE",EDGE,{"disambiguationData":[OSD([subQ2])],"isStart":false}),subQ5],"blendedInto":[subQ5]})])],"isStart":false}),subQ4],"blendedInto":[subQ4]})])],"isStart":false}),subQ7],"blendedInto":[]})])]}),makeQuery(id+"F14.opExtrude","CAP_FACE",FACE,{"disambiguationData":[OSD([subQ3,subQ2,subQ1,subQ0]),TDD([makeQuery(id+"F12.opChamfer","BLEND_FACE",FACE,{"disambiguationData":[OSD([subQ3,subQ2,subQ1,subQ0]),TDD([subQ7])]})])],"isStart":false})]})])],"isStart":false})])]});}
            var Q1;
            {var subQ0=sQuery(id+"F2.wireOp",EDGE,"E10");var subQ1=sQuery(id+"F2.wireOp",EDGE,"E9");var subQ2=sQuery(id+"F2.wireOp",EDGE,"E8");var subQ3=sQuery(id+"F2.wireOp",EDGE,"E7");var subQ4=makeQuery(id+"F5.opExtrude","CAP_FACE",FACE,{"disambiguationData":[OSD([subQ3,subQ2,subQ1,subQ0])],"isStart":false});var subQ5=makeQuery(id+"F8.opChamfer","BLEND_EDGE",EDGE,{"blendedFrom":[makeQuery(id+"F5.opExtrude","CAP_EDGE",EDGE,{"disambiguationData":[OSD([subQ1])],"isStart":false}),subQ4],"blendedInto":[subQ4]});var subQ6=makeQuery(id+"F9.opExtrude","CAP_EDGE",EDGE,{"disambiguationData":[OSD([subQ3,subQ2,subQ1,subQ0]),TDD([subQ5])],"isStart":false});Q1=makeQuery(id+"F22.opExtrude","SWEPT_EDGE",EDGE,{"disambiguationData":[OSD([subQ3,subQ2,subQ1,subQ0]),TDD([makeQuery(id+"F18.opExtrude","CAP_VERTEX",VERTEX,{"disambiguationData":[OSD([subQ3,subQ2,subQ1,subQ0]),TDD([makeQuery(id+"F17.opChamfer","BLEND_VERTEX",VERTEX,{"blendedFrom":[makeQuery(id+"F14.opExtrude","CAP_EDGE",EDGE,{"disambiguationData":[OSD([subQ3,subQ2,subQ1,subQ0]),TDD([makeQuery(id+"F10.opChamfer","BLEND_EDGE",EDGE,{"blendedFrom":[subQ6,makeQuery(id+"F9.opExtrude","SWEPT_FACE",FACE,{"disambiguationData":[OSD([subQ3,subQ2,subQ1,subQ0]),TDD([subQ5])]})],"blendedInto":[makeQuery(id+"F9.opExtrude","SWEPT_FACE",FACE,{"disambiguationData":[OSD([subQ3,subQ2,subQ1,subQ0]),TDD([subQ5])]})]})])],"isStart":false}),makeQuery(id+"F14.opExtrude","SWEPT_FACE",FACE,{"disambiguationData":[OSD([subQ3,subQ2,subQ1,subQ0]),TDD([makeQuery(id+"F10.opChamfer","BLEND_EDGE",EDGE,{"blendedFrom":[makeQuery(id+"F9.opExtrude","CAP_EDGE",EDGE,{"disambiguationData":[OSD([subQ3,subQ2,subQ1,subQ0]),TDD([makeQuery(id+"F8.opChamfer","BLEND_EDGE",EDGE,{"blendedFrom":[makeQuery(id+"F5.opExtrude","CAP_EDGE",EDGE,{"disambiguationData":[OSD([subQ2])],"isStart":false}),subQ4],"blendedInto":[subQ4]})])],"isStart":false}),subQ6],"blendedInto":[]})])]}),makeQuery(id+"F14.opExtrude","CAP_FACE",FACE,{"disambiguationData":[OSD([subQ3,subQ2,subQ1,subQ0]),TDD([makeQuery(id+"F10.opChamfer","BLEND_FACE",FACE,{"disambiguationData":[OSD([subQ3,subQ2,subQ1,subQ0]),TDD([subQ6])]})])],"isStart":false})],"blendedInto":[makeQuery(id+"F14.opExtrude","SWEPT_FACE",FACE,{"disambiguationData":[OSD([subQ3,subQ2,subQ1,subQ0]),TDD([makeQuery(id+"F10.opChamfer","BLEND_EDGE",EDGE,{"blendedFrom":[makeQuery(id+"F9.opExtrude","CAP_EDGE",EDGE,{"disambiguationData":[OSD([subQ3,subQ2,subQ1,subQ0]),TDD([makeQuery(id+"F8.opChamfer","BLEND_EDGE",EDGE,{"blendedFrom":[makeQuery(id+"F5.opExtrude","CAP_EDGE",EDGE,{"disambiguationData":[OSD([subQ2])],"isStart":false}),subQ4],"blendedInto":[subQ4]})])],"isStart":false}),subQ6],"blendedInto":[]})])]}),makeQuery(id+"F14.opExtrude","CAP_FACE",FACE,{"disambiguationData":[OSD([subQ3,subQ2,subQ1,subQ0]),TDD([makeQuery(id+"F10.opChamfer","BLEND_FACE",FACE,{"disambiguationData":[OSD([subQ3,subQ2,subQ1,subQ0]),TDD([subQ6])]})])],"isStart":false})]})])],"isStart":false})])]});}
            var Q2;
            {var subQ0=sQuery(id+"F2.wireOp",EDGE,"E9");var subQ1=sQuery(id+"F2.wireOp",EDGE,"E8");Q2=makeQuery(id+"F22.opExtrude","SWEPT_EDGE",EDGE,{"disambiguationData":[OSD([subQ1,subQ0]),TDD([makeQuery(id+"F18.opExtrude","CAP_VERTEX",VERTEX,{"disambiguationData":[OSD([subQ1,subQ0]),TDD([makeQuery(id+"F17.opChamfer","BLEND_VERTEX",VERTEX,{"blendedFrom":[makeQuery(id+"F14.opExtrude","CAP_EDGE",EDGE,{"disambiguationData":[OSD([subQ0])],"isStart":false}),makeQuery(id+"F14.opExtrude","SWEPT_FACE",FACE,{"disambiguationData":[OSD([subQ1,subQ0])]}),makeQuery(id+"F14.opExtrude","CAP_FACE",FACE,{"disambiguationData":[OSD([subQ0])],"isStart":false})],"blendedInto":[makeQuery(id+"F14.opExtrude","SWEPT_FACE",FACE,{"disambiguationData":[OSD([subQ1,subQ0])]}),makeQuery(id+"F14.opExtrude","CAP_FACE",FACE,{"disambiguationData":[OSD([subQ0])],"isStart":false})]})])],"isStart":false})])]});}
            var Q3;
            {var subQ0=sQuery(id+"F2.wireOp",EDGE,"E10");var subQ1=sQuery(id+"F2.wireOp",EDGE,"E7");Q3=makeQuery(id+"F25.opExtrude","SWEPT_EDGE",EDGE,{"disambiguationData":[OSD([subQ1,subQ0]),TDD([makeQuery(id+"F19.opExtrude","CAP_VERTEX",VERTEX,{"disambiguationData":[OSD([subQ1,subQ0]),TDD([makeQuery(id+"F17.opChamfer","BLEND_VERTEX",VERTEX,{"blendedFrom":[makeQuery(id+"F13.opExtrude","CAP_EDGE",EDGE,{"disambiguationData":[OSD([subQ0])],"isStart":false}),makeQuery(id+"F13.opExtrude","SWEPT_FACE",FACE,{"disambiguationData":[OSD([subQ1,subQ0])]}),makeQuery(id+"F13.opExtrude","CAP_FACE",FACE,{"disambiguationData":[OSD([subQ0])],"isStart":false})],"blendedInto":[makeQuery(id+"F13.opExtrude","SWEPT_FACE",FACE,{"disambiguationData":[OSD([subQ1,subQ0])]}),makeQuery(id+"F13.opExtrude","CAP_FACE",FACE,{"disambiguationData":[OSD([subQ0])],"isStart":false})]})])],"isStart":false})])]});}
            var Q4;
            {var subQ0=sQuery(id+"F2.wireOp",EDGE,"E10");var subQ1=sQuery(id+"F2.wireOp",EDGE,"E9");var subQ2=sQuery(id+"F2.wireOp",EDGE,"E8");var subQ3=sQuery(id+"F2.wireOp",EDGE,"E7");var subQ4=makeQuery(id+"F5.opExtrude","CAP_FACE",FACE,{"disambiguationData":[OSD([subQ3,subQ2,subQ1,subQ0])],"isStart":false});var subQ5=makeQuery(id+"F8.opChamfer","BLEND_EDGE",EDGE,{"blendedFrom":[makeQuery(id+"F5.opExtrude","CAP_EDGE",EDGE,{"disambiguationData":[OSD([subQ0])],"isStart":false}),subQ4],"blendedInto":[subQ4]});var subQ6=makeQuery(id+"F9.opExtrude","CAP_EDGE",EDGE,{"disambiguationData":[OSD([subQ3,subQ2,subQ1,subQ0]),TDD([subQ5])],"isStart":false});Q4=makeQuery(id+"F25.opExtrude","SWEPT_EDGE",EDGE,{"disambiguationData":[OSD([subQ3,subQ2,subQ1,subQ0]),TDD([makeQuery(id+"F19.opExtrude","CAP_VERTEX",VERTEX,{"disambiguationData":[OSD([subQ3,subQ2,subQ1,subQ0]),TDD([makeQuery(id+"F17.opChamfer","BLEND_VERTEX",VERTEX,{"blendedFrom":[makeQuery(id+"F13.opExtrude","CAP_EDGE",EDGE,{"disambiguationData":[OSD([subQ3,subQ2,subQ1,subQ0]),TDD([makeQuery(id+"F10.opChamfer","BLEND_EDGE",EDGE,{"blendedFrom":[subQ6,makeQuery(id+"F9.opExtrude","SWEPT_FACE",FACE,{"disambiguationData":[OSD([subQ3,subQ2,subQ1,subQ0]),TDD([subQ5])]})],"blendedInto":[makeQuery(id+"F9.opExtrude","SWEPT_FACE",FACE,{"disambiguationData":[OSD([subQ3,subQ2,subQ1,subQ0]),TDD([subQ5])]})]})])],"isStart":false}),makeQuery(id+"F13.opExtrude","SWEPT_FACE",FACE,{"disambiguationData":[OSD([subQ3,subQ2,subQ1,subQ0]),TDD([makeQuery(id+"F10.opChamfer","BLEND_EDGE",EDGE,{"blendedFrom":[makeQuery(id+"F9.opExtrude","CAP_EDGE",EDGE,{"disambiguationData":[OSD([subQ3,subQ2,subQ1,subQ0]),TDD([makeQuery(id+"F8.opChamfer","BLEND_EDGE",EDGE,{"blendedFrom":[makeQuery(id+"F5.opExtrude","CAP_EDGE",EDGE,{"disambiguationData":[OSD([subQ3])],"isStart":false}),subQ4],"blendedInto":[subQ4]})])],"isStart":false}),subQ6],"blendedInto":[]})])]}),makeQuery(id+"F13.opExtrude","CAP_FACE",FACE,{"disambiguationData":[OSD([subQ3,subQ2,subQ1,subQ0]),TDD([makeQuery(id+"F10.opChamfer","BLEND_FACE",FACE,{"disambiguationData":[OSD([subQ3,subQ2,subQ1,subQ0]),TDD([subQ6])]})])],"isStart":false})],"blendedInto":[makeQuery(id+"F13.opExtrude","SWEPT_FACE",FACE,{"disambiguationData":[OSD([subQ3,subQ2,subQ1,subQ0]),TDD([makeQuery(id+"F10.opChamfer","BLEND_EDGE",EDGE,{"blendedFrom":[makeQuery(id+"F9.opExtrude","CAP_EDGE",EDGE,{"disambiguationData":[OSD([subQ3,subQ2,subQ1,subQ0]),TDD([makeQuery(id+"F8.opChamfer","BLEND_EDGE",EDGE,{"blendedFrom":[makeQuery(id+"F5.opExtrude","CAP_EDGE",EDGE,{"disambiguationData":[OSD([subQ3])],"isStart":false}),subQ4],"blendedInto":[subQ4]})])],"isStart":false}),subQ6],"blendedInto":[]})])]}),makeQuery(id+"F13.opExtrude","CAP_FACE",FACE,{"disambiguationData":[OSD([subQ3,subQ2,subQ1,subQ0]),TDD([makeQuery(id+"F10.opChamfer","BLEND_FACE",FACE,{"disambiguationData":[OSD([subQ3,subQ2,subQ1,subQ0]),TDD([subQ6])]})])],"isStart":false})]})])],"isStart":false})])]});}
            var Q5;
            {var subQ0=sQuery(id+"F2.wireOp",EDGE,"E10");var subQ1=sQuery(id+"F2.wireOp",EDGE,"E9");var subQ2=sQuery(id+"F2.wireOp",EDGE,"E8");var subQ3=sQuery(id+"F2.wireOp",EDGE,"E7");var subQ4=makeQuery(id+"F9.opExtrude","CAP_FACE",FACE,{"disambiguationData":[OSD([subQ3,subQ2,subQ1,subQ0])],"isStart":false});var subQ5=makeQuery(id+"F5.opExtrude","CAP_FACE",FACE,{"disambiguationData":[OSD([subQ3,subQ2,subQ1,subQ0])],"isStart":false});var subQ6=makeQuery(id+"F10.opChamfer","BLEND_EDGE",EDGE,{"blendedFrom":[makeQuery(id+"F9.opExtrude","CAP_EDGE",EDGE,{"disambiguationData":[OSD([subQ3,subQ2,subQ1,subQ0]),TDD([makeQuery(id+"F8.opChamfer","BLEND_EDGE",EDGE,{"blendedFrom":[makeQuery(id+"F5.opExtrude","CAP_EDGE",EDGE,{"disambiguationData":[OSD([subQ0])],"isStart":false}),subQ5],"blendedInto":[subQ5]})])],"isStart":false}),subQ4],"blendedInto":[subQ4]});var subQ7=makeQuery(id+"F11.opExtrude","CAP_EDGE",EDGE,{"disambiguationData":[OSD([subQ3,subQ2,subQ1,subQ0]),TDD([subQ6])],"isStart":false});Q5=makeQuery(id+"F25.opExtrude","SWEPT_EDGE",EDGE,{"disambiguationData":[OSD([subQ3,subQ2,subQ1,subQ0]),TDD([makeQuery(id+"F19.opExtrude","CAP_VERTEX",VERTEX,{"disambiguationData":[OSD([subQ3,subQ2,subQ1,subQ0]),TDD([makeQuery(id+"F17.opChamfer","BLEND_VERTEX",VERTEX,{"blendedFrom":[makeQuery(id+"F13.opExtrude","CAP_EDGE",EDGE,{"disambiguationData":[OSD([subQ3,subQ2,subQ1,subQ0]),TDD([makeQuery(id+"F12.opChamfer","BLEND_EDGE",EDGE,{"blendedFrom":[subQ7,makeQuery(id+"F11.opExtrude","SWEPT_FACE",FACE,{"disambiguationData":[OSD([subQ3,subQ2,subQ1,subQ0]),TDD([subQ6])]})],"blendedInto":[makeQuery(id+"F11.opExtrude","SWEPT_FACE",FACE,{"disambiguationData":[OSD([subQ3,subQ2,subQ1,subQ0]),TDD([subQ6])]})]})])],"isStart":false}),makeQuery(id+"F13.opExtrude","SWEPT_FACE",FACE,{"disambiguationData":[OSD([subQ3,subQ2,subQ1,subQ0]),TDD([makeQuery(id+"F12.opChamfer","BLEND_EDGE",EDGE,{"blendedFrom":[makeQuery(id+"F11.opExtrude","CAP_EDGE",EDGE,{"disambiguationData":[OSD([subQ3,subQ2,subQ1,subQ0]),TDD([makeQuery(id+"F10.opChamfer","BLEND_EDGE",EDGE,{"blendedFrom":[makeQuery(id+"F9.opExtrude","CAP_EDGE",EDGE,{"disambiguationData":[OSD([subQ3,subQ2,subQ1,subQ0]),TDD([makeQuery(id+"F8.opChamfer","BLEND_EDGE",EDGE,{"blendedFrom":[makeQuery(id+"F5.opExtrude","CAP_EDGE",EDGE,{"disambiguationData":[OSD([subQ3])],"isStart":false}),subQ5],"blendedInto":[subQ5]})])],"isStart":false}),subQ4],"blendedInto":[subQ4]})])],"isStart":false}),subQ7],"blendedInto":[]})])]}),makeQuery(id+"F13.opExtrude","CAP_FACE",FACE,{"disambiguationData":[OSD([subQ3,subQ2,subQ1,subQ0]),TDD([makeQuery(id+"F12.opChamfer","BLEND_FACE",FACE,{"disambiguationData":[OSD([subQ3,subQ2,subQ1,subQ0]),TDD([subQ7])]})])],"isStart":false})],"blendedInto":[makeQuery(id+"F13.opExtrude","SWEPT_FACE",FACE,{"disambiguationData":[OSD([subQ3,subQ2,subQ1,subQ0]),TDD([makeQuery(id+"F12.opChamfer","BLEND_EDGE",EDGE,{"blendedFrom":[makeQuery(id+"F11.opExtrude","CAP_EDGE",EDGE,{"disambiguationData":[OSD([subQ3,subQ2,subQ1,subQ0]),TDD([makeQuery(id+"F10.opChamfer","BLEND_EDGE",EDGE,{"blendedFrom":[makeQuery(id+"F9.opExtrude","CAP_EDGE",EDGE,{"disambiguationData":[OSD([subQ3,subQ2,subQ1,subQ0]),TDD([makeQuery(id+"F8.opChamfer","BLEND_EDGE",EDGE,{"blendedFrom":[makeQuery(id+"F5.opExtrude","CAP_EDGE",EDGE,{"disambiguationData":[OSD([subQ3])],"isStart":false}),subQ5],"blendedInto":[subQ5]})])],"isStart":false}),subQ4],"blendedInto":[subQ4]})])],"isStart":false}),subQ7],"blendedInto":[]})])]}),makeQuery(id+"F13.opExtrude","CAP_FACE",FACE,{"disambiguationData":[OSD([subQ3,subQ2,subQ1,subQ0]),TDD([makeQuery(id+"F12.opChamfer","BLEND_FACE",FACE,{"disambiguationData":[OSD([subQ3,subQ2,subQ1,subQ0]),TDD([subQ7])]})])],"isStart":false})]})])],"isStart":false})])]});}
            var Q6;
            {var subQ0=sQuery(id+"F2.wireOp",EDGE,"E10");var subQ1=sQuery(id+"F2.wireOp",EDGE,"E9");var subQ2=sQuery(id+"F2.wireOp",EDGE,"E8");var subQ3=sQuery(id+"F2.wireOp",EDGE,"E7");var subQ4=makeQuery(id+"F9.opExtrude","CAP_FACE",FACE,{"disambiguationData":[OSD([subQ3,subQ2,subQ1,subQ0])],"isStart":false});var subQ5=makeQuery(id+"F5.opExtrude","CAP_FACE",FACE,{"disambiguationData":[OSD([subQ3,subQ2,subQ1,subQ0])],"isStart":false});var subQ6=makeQuery(id+"F10.opChamfer","BLEND_EDGE",EDGE,{"blendedFrom":[makeQuery(id+"F9.opExtrude","CAP_EDGE",EDGE,{"disambiguationData":[OSD([subQ3,subQ2,subQ1,subQ0]),TDD([makeQuery(id+"F8.opChamfer","BLEND_EDGE",EDGE,{"blendedFrom":[makeQuery(id+"F5.opExtrude","CAP_EDGE",EDGE,{"disambiguationData":[OSD([subQ3])],"isStart":false}),subQ5],"blendedInto":[subQ5]})])],"isStart":false}),subQ4],"blendedInto":[subQ4]});var subQ7=makeQuery(id+"F11.opExtrude","CAP_EDGE",EDGE,{"disambiguationData":[OSD([subQ3,subQ2,subQ1,subQ0]),TDD([subQ6])],"isStart":false});var subQ8=makeQuery(id+"F12.opChamfer","BLEND_EDGE",EDGE,{"blendedFrom":[subQ7,makeQuery(id+"F11.opExtrude","CAP_EDGE",EDGE,{"disambiguationData":[OSD([subQ3,subQ2,subQ1,subQ0]),TDD([makeQuery(id+"F10.opChamfer","BLEND_EDGE",EDGE,{"blendedFrom":[makeQuery(id+"F9.opExtrude","CAP_EDGE",EDGE,{"disambiguationData":[OSD([subQ3,subQ2,subQ1,subQ0]),TDD([makeQuery(id+"F8.opChamfer","BLEND_EDGE",EDGE,{"blendedFrom":[makeQuery(id+"F5.opExtrude","CAP_EDGE",EDGE,{"disambiguationData":[OSD([subQ0])],"isStart":false}),subQ5],"blendedInto":[subQ5]})])],"isStart":false}),subQ4],"blendedInto":[subQ4]})])],"isStart":false})],"blendedInto":[]});Q6=makeQuery(id+"F24.opExtrude","SWEPT_EDGE",EDGE,{"disambiguationData":[OSD([subQ3,subQ2,subQ1,subQ0]),TDD([makeQuery(id+"F20.opExtrude","CAP_VERTEX",VERTEX,{"disambiguationData":[OSD([subQ3,subQ2,subQ1,subQ0]),TDD([makeQuery(id+"F17.opChamfer","BLEND_VERTEX",VERTEX,{"blendedFrom":[makeQuery(id+"F15.opExtrude","CAP_EDGE",EDGE,{"disambiguationData":[OSD([subQ3,subQ2,subQ1,subQ0]),TDD([makeQuery(id+"F12.opChamfer","BLEND_EDGE",EDGE,{"blendedFrom":[subQ7,makeQuery(id+"F11.opExtrude","SWEPT_FACE",FACE,{"disambiguationData":[OSD([subQ3,subQ2,subQ1,subQ0]),TDD([subQ6])]})],"blendedInto":[makeQuery(id+"F11.opExtrude","SWEPT_FACE",FACE,{"disambiguationData":[OSD([subQ3,subQ2,subQ1,subQ0]),TDD([subQ6])]})]})])],"isStart":false}),makeQuery(id+"F15.opExtrude","CAP_FACE",FACE,{"disambiguationData":[OSD([subQ3,subQ2,subQ1,subQ0]),TDD([makeQuery(id+"F12.opChamfer","BLEND_FACE",FACE,{"disambiguationData":[OSD([subQ3,subQ2,subQ1,subQ0]),TDD([subQ7])]})])],"isStart":false}),makeQuery(id+"F15.opExtrude","SWEPT_FACE",FACE,{"disambiguationData":[OSD([subQ3,subQ2,subQ1,subQ0]),TDD([makeQuery(id+"F13.boolean.opBoolean","MERGE",EDGE,{"derivedFrom":[subQ8,makeQuery(id+"F13.opExtrude","CAP_EDGE",EDGE,{"disambiguationData":[OSD([subQ3,subQ2,subQ1,subQ0]),TDD([subQ8])],"isStart":true})]})])]})],"blendedInto":[makeQuery(id+"F15.opExtrude","CAP_FACE",FACE,{"disambiguationData":[OSD([subQ3,subQ2,subQ1,subQ0]),TDD([makeQuery(id+"F12.opChamfer","BLEND_FACE",FACE,{"disambiguationData":[OSD([subQ3,subQ2,subQ1,subQ0]),TDD([subQ7])]})])],"isStart":false}),makeQuery(id+"F15.opExtrude","SWEPT_FACE",FACE,{"disambiguationData":[OSD([subQ3,subQ2,subQ1,subQ0]),TDD([makeQuery(id+"F13.boolean.opBoolean","MERGE",EDGE,{"derivedFrom":[subQ8,makeQuery(id+"F13.opExtrude","CAP_EDGE",EDGE,{"disambiguationData":[OSD([subQ3,subQ2,subQ1,subQ0]),TDD([subQ8])],"isStart":true})]})])]})]})])],"isStart":false})])]});}
            var Q7;
            {var subQ0=sQuery(id+"F2.wireOp",EDGE,"E10");var subQ1=sQuery(id+"F2.wireOp",EDGE,"E9");var subQ2=sQuery(id+"F2.wireOp",EDGE,"E8");var subQ3=sQuery(id+"F2.wireOp",EDGE,"E7");var subQ4=makeQuery(id+"F5.opExtrude","CAP_FACE",FACE,{"disambiguationData":[OSD([subQ3,subQ2,subQ1,subQ0])],"isStart":false});var subQ5=makeQuery(id+"F8.opChamfer","BLEND_EDGE",EDGE,{"blendedFrom":[makeQuery(id+"F5.opExtrude","CAP_EDGE",EDGE,{"disambiguationData":[OSD([subQ3])],"isStart":false}),subQ4],"blendedInto":[subQ4]});var subQ6=makeQuery(id+"F9.opExtrude","CAP_EDGE",EDGE,{"disambiguationData":[OSD([subQ3,subQ2,subQ1,subQ0]),TDD([subQ5])],"isStart":false});var subQ7=makeQuery(id+"F10.opChamfer","BLEND_EDGE",EDGE,{"blendedFrom":[subQ6,makeQuery(id+"F9.opExtrude","CAP_EDGE",EDGE,{"disambiguationData":[OSD([subQ3,subQ2,subQ1,subQ0]),TDD([makeQuery(id+"F8.opChamfer","BLEND_EDGE",EDGE,{"blendedFrom":[makeQuery(id+"F5.opExtrude","CAP_EDGE",EDGE,{"disambiguationData":[OSD([subQ0])],"isStart":false}),subQ4],"blendedInto":[subQ4]})])],"isStart":false})],"blendedInto":[]});Q7=makeQuery(id+"F24.opExtrude","SWEPT_EDGE",EDGE,{"disambiguationData":[OSD([subQ3,subQ2,subQ1,subQ0]),TDD([makeQuery(id+"F20.opExtrude","CAP_VERTEX",VERTEX,{"disambiguationData":[OSD([subQ3,subQ2,subQ1,subQ0]),TDD([makeQuery(id+"F17.opChamfer","BLEND_VERTEX",VERTEX,{"blendedFrom":[makeQuery(id+"F15.opExtrude","CAP_EDGE",EDGE,{"disambiguationData":[OSD([subQ3,subQ2,subQ1,subQ0]),TDD([makeQuery(id+"F10.opChamfer","BLEND_EDGE",EDGE,{"blendedFrom":[subQ6,makeQuery(id+"F9.opExtrude","SWEPT_FACE",FACE,{"disambiguationData":[OSD([subQ3,subQ2,subQ1,subQ0]),TDD([subQ5])]})],"blendedInto":[makeQuery(id+"F9.opExtrude","SWEPT_FACE",FACE,{"disambiguationData":[OSD([subQ3,subQ2,subQ1,subQ0]),TDD([subQ5])]})]})])],"isStart":false}),makeQuery(id+"F15.opExtrude","CAP_FACE",FACE,{"disambiguationData":[OSD([subQ3,subQ2,subQ1,subQ0]),TDD([makeQuery(id+"F10.opChamfer","BLEND_FACE",FACE,{"disambiguationData":[OSD([subQ3,subQ2,subQ1,subQ0]),TDD([subQ6])]})])],"isStart":false}),makeQuery(id+"F15.opExtrude","SWEPT_FACE",FACE,{"disambiguationData":[OSD([subQ3,subQ2,subQ1,subQ0]),TDD([makeQuery(id+"F13.boolean.opBoolean","MERGE",EDGE,{"derivedFrom":[subQ7,makeQuery(id+"F13.opExtrude","CAP_EDGE",EDGE,{"disambiguationData":[OSD([subQ3,subQ2,subQ1,subQ0]),TDD([subQ7])],"isStart":true})]})])]})],"blendedInto":[makeQuery(id+"F15.opExtrude","CAP_FACE",FACE,{"disambiguationData":[OSD([subQ3,subQ2,subQ1,subQ0]),TDD([makeQuery(id+"F10.opChamfer","BLEND_FACE",FACE,{"disambiguationData":[OSD([subQ3,subQ2,subQ1,subQ0]),TDD([subQ6])]})])],"isStart":false}),makeQuery(id+"F15.opExtrude","SWEPT_FACE",FACE,{"disambiguationData":[OSD([subQ3,subQ2,subQ1,subQ0]),TDD([makeQuery(id+"F13.boolean.opBoolean","MERGE",EDGE,{"derivedFrom":[subQ7,makeQuery(id+"F13.opExtrude","CAP_EDGE",EDGE,{"disambiguationData":[OSD([subQ3,subQ2,subQ1,subQ0]),TDD([subQ7])],"isStart":true})]})])]})]})])],"isStart":false})])]});}
            var Q8;
            {var subQ0=sQuery(id+"F2.wireOp",EDGE,"E10");var subQ1=sQuery(id+"F2.wireOp",EDGE,"E7");Q8=makeQuery(id+"F24.opExtrude","SWEPT_EDGE",EDGE,{"disambiguationData":[OSD([subQ1,subQ0]),TDD([makeQuery(id+"F20.opExtrude","CAP_VERTEX",VERTEX,{"disambiguationData":[OSD([subQ1,subQ0]),TDD([makeQuery(id+"F17.opChamfer","BLEND_VERTEX",VERTEX,{"blendedFrom":[makeQuery(id+"F15.opExtrude","CAP_EDGE",EDGE,{"disambiguationData":[OSD([subQ1])],"isStart":false}),makeQuery(id+"F15.opExtrude","CAP_FACE",FACE,{"disambiguationData":[OSD([subQ1])],"isStart":false}),makeQuery(id+"F15.opExtrude","SWEPT_FACE",FACE,{"disambiguationData":[OSD([subQ1,subQ0])]})],"blendedInto":[makeQuery(id+"F15.opExtrude","CAP_FACE",FACE,{"disambiguationData":[OSD([subQ1])],"isStart":false}),makeQuery(id+"F15.opExtrude","SWEPT_FACE",FACE,{"disambiguationData":[OSD([subQ1,subQ0])]})]})])],"isStart":false})])]});}
            var Q9;
            {var subQ0=sQuery(id+"F2.wireOp",EDGE,"E10");var subQ1=sQuery(id+"F2.wireOp",EDGE,"E9");var subQ2=sQuery(id+"F2.wireOp",EDGE,"E8");var subQ3=sQuery(id+"F2.wireOp",EDGE,"E7");var subQ4=makeQuery(id+"F9.opExtrude","CAP_FACE",FACE,{"disambiguationData":[OSD([subQ3,subQ2,subQ1,subQ0])],"isStart":false});var subQ5=makeQuery(id+"F5.opExtrude","CAP_FACE",FACE,{"disambiguationData":[OSD([subQ3,subQ2,subQ1,subQ0])],"isStart":false});var subQ6=makeQuery(id+"F10.opChamfer","BLEND_EDGE",EDGE,{"blendedFrom":[makeQuery(id+"F9.opExtrude","CAP_EDGE",EDGE,{"disambiguationData":[OSD([subQ3,subQ2,subQ1,subQ0]),TDD([makeQuery(id+"F8.opChamfer","BLEND_EDGE",EDGE,{"blendedFrom":[makeQuery(id+"F5.opExtrude","CAP_EDGE",EDGE,{"disambiguationData":[OSD([subQ2])],"isStart":false}),subQ5],"blendedInto":[subQ5]})])],"isStart":false}),subQ4],"blendedInto":[subQ4]});var subQ7=makeQuery(id+"F11.opExtrude","CAP_EDGE",EDGE,{"disambiguationData":[OSD([subQ3,subQ2,subQ1,subQ0]),TDD([subQ6])],"isStart":false});var subQ8=makeQuery(id+"F12.opChamfer","BLEND_EDGE",EDGE,{"blendedFrom":[subQ7,makeQuery(id+"F11.opExtrude","CAP_EDGE",EDGE,{"disambiguationData":[OSD([subQ3,subQ2,subQ1,subQ0]),TDD([makeQuery(id+"F10.opChamfer","BLEND_EDGE",EDGE,{"blendedFrom":[makeQuery(id+"F9.opExtrude","CAP_EDGE",EDGE,{"disambiguationData":[OSD([subQ3,subQ2,subQ1,subQ0]),TDD([makeQuery(id+"F8.opChamfer","BLEND_EDGE",EDGE,{"blendedFrom":[makeQuery(id+"F5.opExtrude","CAP_EDGE",EDGE,{"disambiguationData":[OSD([subQ1])],"isStart":false}),subQ5],"blendedInto":[subQ5]})])],"isStart":false}),subQ4],"blendedInto":[subQ4]})])],"isStart":false})],"blendedInto":[]});Q9=makeQuery(id+"F23.opExtrude","SWEPT_EDGE",EDGE,{"disambiguationData":[OSD([subQ3,subQ2,subQ1,subQ0]),TDD([makeQuery(id+"F21.opExtrude","CAP_VERTEX",VERTEX,{"disambiguationData":[OSD([subQ3,subQ2,subQ1,subQ0]),TDD([makeQuery(id+"F17.opChamfer","BLEND_VERTEX",VERTEX,{"blendedFrom":[makeQuery(id+"F16.opExtrude","CAP_EDGE",EDGE,{"disambiguationData":[OSD([subQ3,subQ2,subQ1,subQ0]),TDD([makeQuery(id+"F12.opChamfer","BLEND_EDGE",EDGE,{"blendedFrom":[subQ7,makeQuery(id+"F11.opExtrude","SWEPT_FACE",FACE,{"disambiguationData":[OSD([subQ3,subQ2,subQ1,subQ0]),TDD([subQ6])]})],"blendedInto":[makeQuery(id+"F11.opExtrude","SWEPT_FACE",FACE,{"disambiguationData":[OSD([subQ3,subQ2,subQ1,subQ0]),TDD([subQ6])]})]})])],"isStart":false}),makeQuery(id+"F16.opExtrude","CAP_FACE",FACE,{"disambiguationData":[OSD([subQ3,subQ2,subQ1,subQ0]),TDD([makeQuery(id+"F12.opChamfer","BLEND_FACE",FACE,{"disambiguationData":[OSD([subQ3,subQ2,subQ1,subQ0]),TDD([subQ7])]})])],"isStart":false}),makeQuery(id+"F16.opExtrude","SWEPT_FACE",FACE,{"disambiguationData":[OSD([subQ3,subQ2,subQ1,subQ0]),TDD([makeQuery(id+"F14.boolean.opBoolean","MERGE",EDGE,{"derivedFrom":[subQ8,makeQuery(id+"F14.opExtrude","CAP_EDGE",EDGE,{"disambiguationData":[OSD([subQ3,subQ2,subQ1,subQ0]),TDD([subQ8])],"isStart":true})]})])]})],"blendedInto":[makeQuery(id+"F16.opExtrude","CAP_FACE",FACE,{"disambiguationData":[OSD([subQ3,subQ2,subQ1,subQ0]),TDD([makeQuery(id+"F12.opChamfer","BLEND_FACE",FACE,{"disambiguationData":[OSD([subQ3,subQ2,subQ1,subQ0]),TDD([subQ7])]})])],"isStart":false}),makeQuery(id+"F16.opExtrude","SWEPT_FACE",FACE,{"disambiguationData":[OSD([subQ3,subQ2,subQ1,subQ0]),TDD([makeQuery(id+"F14.boolean.opBoolean","MERGE",EDGE,{"derivedFrom":[subQ8,makeQuery(id+"F14.opExtrude","CAP_EDGE",EDGE,{"disambiguationData":[OSD([subQ3,subQ2,subQ1,subQ0]),TDD([subQ8])],"isStart":true})]})])]})]})])],"isStart":false})])]});}
            var Q10;
            {var subQ0=sQuery(id+"F2.wireOp",EDGE,"E10");var subQ1=sQuery(id+"F2.wireOp",EDGE,"E9");var subQ2=sQuery(id+"F2.wireOp",EDGE,"E8");var subQ3=sQuery(id+"F2.wireOp",EDGE,"E7");var subQ4=makeQuery(id+"F5.opExtrude","CAP_FACE",FACE,{"disambiguationData":[OSD([subQ3,subQ2,subQ1,subQ0])],"isStart":false});var subQ5=makeQuery(id+"F8.opChamfer","BLEND_EDGE",EDGE,{"blendedFrom":[makeQuery(id+"F5.opExtrude","CAP_EDGE",EDGE,{"disambiguationData":[OSD([subQ2])],"isStart":false}),subQ4],"blendedInto":[subQ4]});var subQ6=makeQuery(id+"F9.opExtrude","CAP_EDGE",EDGE,{"disambiguationData":[OSD([subQ3,subQ2,subQ1,subQ0]),TDD([subQ5])],"isStart":false});var subQ7=makeQuery(id+"F10.opChamfer","BLEND_EDGE",EDGE,{"blendedFrom":[subQ6,makeQuery(id+"F9.opExtrude","CAP_EDGE",EDGE,{"disambiguationData":[OSD([subQ3,subQ2,subQ1,subQ0]),TDD([makeQuery(id+"F8.opChamfer","BLEND_EDGE",EDGE,{"blendedFrom":[makeQuery(id+"F5.opExtrude","CAP_EDGE",EDGE,{"disambiguationData":[OSD([subQ1])],"isStart":false}),subQ4],"blendedInto":[subQ4]})])],"isStart":false})],"blendedInto":[]});Q10=makeQuery(id+"F23.opExtrude","SWEPT_EDGE",EDGE,{"disambiguationData":[OSD([subQ3,subQ2,subQ1,subQ0]),TDD([makeQuery(id+"F21.opExtrude","CAP_VERTEX",VERTEX,{"disambiguationData":[OSD([subQ3,subQ2,subQ1,subQ0]),TDD([makeQuery(id+"F17.opChamfer","BLEND_VERTEX",VERTEX,{"blendedFrom":[makeQuery(id+"F16.opExtrude","CAP_EDGE",EDGE,{"disambiguationData":[OSD([subQ3,subQ2,subQ1,subQ0]),TDD([makeQuery(id+"F10.opChamfer","BLEND_EDGE",EDGE,{"blendedFrom":[subQ6,makeQuery(id+"F9.opExtrude","SWEPT_FACE",FACE,{"disambiguationData":[OSD([subQ3,subQ2,subQ1,subQ0]),TDD([subQ5])]})],"blendedInto":[makeQuery(id+"F9.opExtrude","SWEPT_FACE",FACE,{"disambiguationData":[OSD([subQ3,subQ2,subQ1,subQ0]),TDD([subQ5])]})]})])],"isStart":false}),makeQuery(id+"F16.opExtrude","CAP_FACE",FACE,{"disambiguationData":[OSD([subQ3,subQ2,subQ1,subQ0]),TDD([makeQuery(id+"F10.opChamfer","BLEND_FACE",FACE,{"disambiguationData":[OSD([subQ3,subQ2,subQ1,subQ0]),TDD([subQ6])]})])],"isStart":false}),makeQuery(id+"F16.opExtrude","SWEPT_FACE",FACE,{"disambiguationData":[OSD([subQ3,subQ2,subQ1,subQ0]),TDD([makeQuery(id+"F14.boolean.opBoolean","MERGE",EDGE,{"derivedFrom":[subQ7,makeQuery(id+"F14.opExtrude","CAP_EDGE",EDGE,{"disambiguationData":[OSD([subQ3,subQ2,subQ1,subQ0]),TDD([subQ7])],"isStart":true})]})])]})],"blendedInto":[makeQuery(id+"F16.opExtrude","CAP_FACE",FACE,{"disambiguationData":[OSD([subQ3,subQ2,subQ1,subQ0]),TDD([makeQuery(id+"F10.opChamfer","BLEND_FACE",FACE,{"disambiguationData":[OSD([subQ3,subQ2,subQ1,subQ0]),TDD([subQ6])]})])],"isStart":false}),makeQuery(id+"F16.opExtrude","SWEPT_FACE",FACE,{"disambiguationData":[OSD([subQ3,subQ2,subQ1,subQ0]),TDD([makeQuery(id+"F14.boolean.opBoolean","MERGE",EDGE,{"derivedFrom":[subQ7,makeQuery(id+"F14.opExtrude","CAP_EDGE",EDGE,{"disambiguationData":[OSD([subQ3,subQ2,subQ1,subQ0]),TDD([subQ7])],"isStart":true})]})])]})]})])],"isStart":false})])]});}
            var Q11;
            {var subQ0=sQuery(id+"F2.wireOp",EDGE,"E9");var subQ1=sQuery(id+"F2.wireOp",EDGE,"E8");Q11=makeQuery(id+"F23.opExtrude","SWEPT_EDGE",EDGE,{"disambiguationData":[OSD([subQ1,subQ0]),TDD([makeQuery(id+"F21.opExtrude","CAP_VERTEX",VERTEX,{"disambiguationData":[OSD([subQ1,subQ0]),TDD([makeQuery(id+"F17.opChamfer","BLEND_VERTEX",VERTEX,{"blendedFrom":[makeQuery(id+"F16.opExtrude","CAP_EDGE",EDGE,{"disambiguationData":[OSD([subQ1])],"isStart":false}),makeQuery(id+"F16.opExtrude","CAP_FACE",FACE,{"disambiguationData":[OSD([subQ1])],"isStart":false}),makeQuery(id+"F16.opExtrude","SWEPT_FACE",FACE,{"disambiguationData":[OSD([subQ1,subQ0])]})],"blendedInto":[makeQuery(id+"F16.opExtrude","CAP_FACE",FACE,{"disambiguationData":[OSD([subQ1])],"isStart":false}),makeQuery(id+"F16.opExtrude","SWEPT_FACE",FACE,{"disambiguationData":[OSD([subQ1,subQ0])]})]})])],"isStart":false})])]});}
            chamfer(context, id + "F26", {"entities" : qUnion([Q0, Q1, Q2, Q3, Q4, Q5, Q6, Q7, Q8, Q9, Q10, Q11]), "width" : 5.08 * mm, "tangentPropagation" : true});
        }
        {
            var Q0;
            {var subQ0=sQuery(id+"F2.wireOp",EDGE,"E9");var subQ1=sQuery(id+"F2.wireOp",EDGE,"E8");Q0=makeQuery(id+"F26.opChamfer","BLEND_FACE",FACE,{"disambiguationData":[OSD([subQ1,subQ0]),TDD([makeQuery(id+"F22.opExtrude","SWEPT_EDGE",EDGE,{"disambiguationData":[OSD([subQ1,subQ0]),TDD([makeQuery(id+"F18.opExtrude","CAP_VERTEX",VERTEX,{"disambiguationData":[OSD([subQ1,subQ0]),TDD([makeQuery(id+"F17.opChamfer","BLEND_VERTEX",VERTEX,{"blendedFrom":[makeQuery(id+"F14.opExtrude","CAP_EDGE",EDGE,{"disambiguationData":[OSD([subQ0])],"isStart":false}),makeQuery(id+"F14.opExtrude","SWEPT_FACE",FACE,{"disambiguationData":[OSD([subQ1,subQ0])]}),makeQuery(id+"F14.opExtrude","CAP_FACE",FACE,{"disambiguationData":[OSD([subQ0])],"isStart":false})],"blendedInto":[makeQuery(id+"F14.opExtrude","SWEPT_FACE",FACE,{"disambiguationData":[OSD([subQ1,subQ0])]}),makeQuery(id+"F14.opExtrude","CAP_FACE",FACE,{"disambiguationData":[OSD([subQ0])],"isStart":false})]})])],"isStart":false})])]})])]});}
            var Q1;
            {var subQ0=sQuery(id+"F2.wireOp",EDGE,"E10");var subQ1=sQuery(id+"F2.wireOp",EDGE,"E9");var subQ2=sQuery(id+"F2.wireOp",EDGE,"E8");var subQ3=sQuery(id+"F2.wireOp",EDGE,"E7");var subQ4=makeQuery(id+"F5.opExtrude","CAP_FACE",FACE,{"disambiguationData":[OSD([subQ3,subQ2,subQ1,subQ0])],"isStart":false});var subQ5=makeQuery(id+"F8.opChamfer","BLEND_EDGE",EDGE,{"blendedFrom":[makeQuery(id+"F5.opExtrude","CAP_EDGE",EDGE,{"disambiguationData":[OSD([subQ1])],"isStart":false}),subQ4],"blendedInto":[subQ4]});var subQ6=makeQuery(id+"F9.opExtrude","CAP_EDGE",EDGE,{"disambiguationData":[OSD([subQ3,subQ2,subQ1,subQ0]),TDD([subQ5])],"isStart":false});Q1=makeQuery(id+"F26.opChamfer","BLEND_FACE",FACE,{"disambiguationData":[OSD([subQ3,subQ2,subQ1,subQ0]),TDD([makeQuery(id+"F22.opExtrude","SWEPT_EDGE",EDGE,{"disambiguationData":[OSD([subQ3,subQ2,subQ1,subQ0]),TDD([makeQuery(id+"F18.opExtrude","CAP_VERTEX",VERTEX,{"disambiguationData":[OSD([subQ3,subQ2,subQ1,subQ0]),TDD([makeQuery(id+"F17.opChamfer","BLEND_VERTEX",VERTEX,{"blendedFrom":[makeQuery(id+"F14.opExtrude","CAP_EDGE",EDGE,{"disambiguationData":[OSD([subQ3,subQ2,subQ1,subQ0]),TDD([makeQuery(id+"F10.opChamfer","BLEND_EDGE",EDGE,{"blendedFrom":[subQ6,makeQuery(id+"F9.opExtrude","SWEPT_FACE",FACE,{"disambiguationData":[OSD([subQ3,subQ2,subQ1,subQ0]),TDD([subQ5])]})],"blendedInto":[makeQuery(id+"F9.opExtrude","SWEPT_FACE",FACE,{"disambiguationData":[OSD([subQ3,subQ2,subQ1,subQ0]),TDD([subQ5])]})]})])],"isStart":false}),makeQuery(id+"F14.opExtrude","SWEPT_FACE",FACE,{"disambiguationData":[OSD([subQ3,subQ2,subQ1,subQ0]),TDD([makeQuery(id+"F10.opChamfer","BLEND_EDGE",EDGE,{"blendedFrom":[makeQuery(id+"F9.opExtrude","CAP_EDGE",EDGE,{"disambiguationData":[OSD([subQ3,subQ2,subQ1,subQ0]),TDD([makeQuery(id+"F8.opChamfer","BLEND_EDGE",EDGE,{"blendedFrom":[makeQuery(id+"F5.opExtrude","CAP_EDGE",EDGE,{"disambiguationData":[OSD([subQ2])],"isStart":false}),subQ4],"blendedInto":[subQ4]})])],"isStart":false}),subQ6],"blendedInto":[]})])]}),makeQuery(id+"F14.opExtrude","CAP_FACE",FACE,{"disambiguationData":[OSD([subQ3,subQ2,subQ1,subQ0]),TDD([makeQuery(id+"F10.opChamfer","BLEND_FACE",FACE,{"disambiguationData":[OSD([subQ3,subQ2,subQ1,subQ0]),TDD([subQ6])]})])],"isStart":false})],"blendedInto":[makeQuery(id+"F14.opExtrude","SWEPT_FACE",FACE,{"disambiguationData":[OSD([subQ3,subQ2,subQ1,subQ0]),TDD([makeQuery(id+"F10.opChamfer","BLEND_EDGE",EDGE,{"blendedFrom":[makeQuery(id+"F9.opExtrude","CAP_EDGE",EDGE,{"disambiguationData":[OSD([subQ3,subQ2,subQ1,subQ0]),TDD([makeQuery(id+"F8.opChamfer","BLEND_EDGE",EDGE,{"blendedFrom":[makeQuery(id+"F5.opExtrude","CAP_EDGE",EDGE,{"disambiguationData":[OSD([subQ2])],"isStart":false}),subQ4],"blendedInto":[subQ4]})])],"isStart":false}),subQ6],"blendedInto":[]})])]}),makeQuery(id+"F14.opExtrude","CAP_FACE",FACE,{"disambiguationData":[OSD([subQ3,subQ2,subQ1,subQ0]),TDD([makeQuery(id+"F10.opChamfer","BLEND_FACE",FACE,{"disambiguationData":[OSD([subQ3,subQ2,subQ1,subQ0]),TDD([subQ6])]})])],"isStart":false})]})])],"isStart":false})])]})])]});}
            var Q2;
            {var subQ0=sQuery(id+"F2.wireOp",EDGE,"E10");var subQ1=sQuery(id+"F2.wireOp",EDGE,"E9");var subQ2=sQuery(id+"F2.wireOp",EDGE,"E8");var subQ3=sQuery(id+"F2.wireOp",EDGE,"E7");var subQ4=makeQuery(id+"F9.opExtrude","CAP_FACE",FACE,{"disambiguationData":[OSD([subQ3,subQ2,subQ1,subQ0])],"isStart":false});var subQ5=makeQuery(id+"F5.opExtrude","CAP_FACE",FACE,{"disambiguationData":[OSD([subQ3,subQ2,subQ1,subQ0])],"isStart":false});var subQ6=makeQuery(id+"F10.opChamfer","BLEND_EDGE",EDGE,{"blendedFrom":[makeQuery(id+"F9.opExtrude","CAP_EDGE",EDGE,{"disambiguationData":[OSD([subQ3,subQ2,subQ1,subQ0]),TDD([makeQuery(id+"F8.opChamfer","BLEND_EDGE",EDGE,{"blendedFrom":[makeQuery(id+"F5.opExtrude","CAP_EDGE",EDGE,{"disambiguationData":[OSD([subQ1])],"isStart":false}),subQ5],"blendedInto":[subQ5]})])],"isStart":false}),subQ4],"blendedInto":[subQ4]});var subQ7=makeQuery(id+"F11.opExtrude","CAP_EDGE",EDGE,{"disambiguationData":[OSD([subQ3,subQ2,subQ1,subQ0]),TDD([subQ6])],"isStart":false});Q2=makeQuery(id+"F26.opChamfer","BLEND_FACE",FACE,{"disambiguationData":[OSD([subQ3,subQ2,subQ1,subQ0]),TDD([makeQuery(id+"F22.opExtrude","SWEPT_EDGE",EDGE,{"disambiguationData":[OSD([subQ3,subQ2,subQ1,subQ0]),TDD([makeQuery(id+"F18.opExtrude","CAP_VERTEX",VERTEX,{"disambiguationData":[OSD([subQ3,subQ2,subQ1,subQ0]),TDD([makeQuery(id+"F17.opChamfer","BLEND_VERTEX",VERTEX,{"blendedFrom":[makeQuery(id+"F14.opExtrude","CAP_EDGE",EDGE,{"disambiguationData":[OSD([subQ3,subQ2,subQ1,subQ0]),TDD([makeQuery(id+"F12.opChamfer","BLEND_EDGE",EDGE,{"blendedFrom":[subQ7,makeQuery(id+"F11.opExtrude","SWEPT_FACE",FACE,{"disambiguationData":[OSD([subQ3,subQ2,subQ1,subQ0]),TDD([subQ6])]})],"blendedInto":[makeQuery(id+"F11.opExtrude","SWEPT_FACE",FACE,{"disambiguationData":[OSD([subQ3,subQ2,subQ1,subQ0]),TDD([subQ6])]})]})])],"isStart":false}),makeQuery(id+"F14.opExtrude","SWEPT_FACE",FACE,{"disambiguationData":[OSD([subQ3,subQ2,subQ1,subQ0]),TDD([makeQuery(id+"F12.opChamfer","BLEND_EDGE",EDGE,{"blendedFrom":[makeQuery(id+"F11.opExtrude","CAP_EDGE",EDGE,{"disambiguationData":[OSD([subQ3,subQ2,subQ1,subQ0]),TDD([makeQuery(id+"F10.opChamfer","BLEND_EDGE",EDGE,{"blendedFrom":[makeQuery(id+"F9.opExtrude","CAP_EDGE",EDGE,{"disambiguationData":[OSD([subQ3,subQ2,subQ1,subQ0]),TDD([makeQuery(id+"F8.opChamfer","BLEND_EDGE",EDGE,{"blendedFrom":[makeQuery(id+"F5.opExtrude","CAP_EDGE",EDGE,{"disambiguationData":[OSD([subQ2])],"isStart":false}),subQ5],"blendedInto":[subQ5]})])],"isStart":false}),subQ4],"blendedInto":[subQ4]})])],"isStart":false}),subQ7],"blendedInto":[]})])]}),makeQuery(id+"F14.opExtrude","CAP_FACE",FACE,{"disambiguationData":[OSD([subQ3,subQ2,subQ1,subQ0]),TDD([makeQuery(id+"F12.opChamfer","BLEND_FACE",FACE,{"disambiguationData":[OSD([subQ3,subQ2,subQ1,subQ0]),TDD([subQ7])]})])],"isStart":false})],"blendedInto":[makeQuery(id+"F14.opExtrude","SWEPT_FACE",FACE,{"disambiguationData":[OSD([subQ3,subQ2,subQ1,subQ0]),TDD([makeQuery(id+"F12.opChamfer","BLEND_EDGE",EDGE,{"blendedFrom":[makeQuery(id+"F11.opExtrude","CAP_EDGE",EDGE,{"disambiguationData":[OSD([subQ3,subQ2,subQ1,subQ0]),TDD([makeQuery(id+"F10.opChamfer","BLEND_EDGE",EDGE,{"blendedFrom":[makeQuery(id+"F9.opExtrude","CAP_EDGE",EDGE,{"disambiguationData":[OSD([subQ3,subQ2,subQ1,subQ0]),TDD([makeQuery(id+"F8.opChamfer","BLEND_EDGE",EDGE,{"blendedFrom":[makeQuery(id+"F5.opExtrude","CAP_EDGE",EDGE,{"disambiguationData":[OSD([subQ2])],"isStart":false}),subQ5],"blendedInto":[subQ5]})])],"isStart":false}),subQ4],"blendedInto":[subQ4]})])],"isStart":false}),subQ7],"blendedInto":[]})])]}),makeQuery(id+"F14.opExtrude","CAP_FACE",FACE,{"disambiguationData":[OSD([subQ3,subQ2,subQ1,subQ0]),TDD([makeQuery(id+"F12.opChamfer","BLEND_FACE",FACE,{"disambiguationData":[OSD([subQ3,subQ2,subQ1,subQ0]),TDD([subQ7])]})])],"isStart":false})]})])],"isStart":false})])]})])]});}
            extrude(context, id + "F27", {"entities" : qUnion([Q0, Q1, Q2]), "operationType" : NewBodyOperationType.ADD, "depth" : 25.4 * mm});
        }
        {
            var Q0;
            {var subQ0=sQuery(id+"F2.wireOp",EDGE,"E10");var subQ1=sQuery(id+"F2.wireOp",EDGE,"E7");Q0=makeQuery(id+"F26.opChamfer","BLEND_FACE",FACE,{"disambiguationData":[OSD([subQ1,subQ0]),TDD([makeQuery(id+"F25.opExtrude","SWEPT_EDGE",EDGE,{"disambiguationData":[OSD([subQ1,subQ0]),TDD([makeQuery(id+"F19.opExtrude","CAP_VERTEX",VERTEX,{"disambiguationData":[OSD([subQ1,subQ0]),TDD([makeQuery(id+"F17.opChamfer","BLEND_VERTEX",VERTEX,{"blendedFrom":[makeQuery(id+"F13.opExtrude","CAP_EDGE",EDGE,{"disambiguationData":[OSD([subQ0])],"isStart":false}),makeQuery(id+"F13.opExtrude","SWEPT_FACE",FACE,{"disambiguationData":[OSD([subQ1,subQ0])]}),makeQuery(id+"F13.opExtrude","CAP_FACE",FACE,{"disambiguationData":[OSD([subQ0])],"isStart":false})],"blendedInto":[makeQuery(id+"F13.opExtrude","SWEPT_FACE",FACE,{"disambiguationData":[OSD([subQ1,subQ0])]}),makeQuery(id+"F13.opExtrude","CAP_FACE",FACE,{"disambiguationData":[OSD([subQ0])],"isStart":false})]})])],"isStart":false})])]})])]});}
            var Q1;
            {var subQ0=sQuery(id+"F2.wireOp",EDGE,"E10");var subQ1=sQuery(id+"F2.wireOp",EDGE,"E9");var subQ2=sQuery(id+"F2.wireOp",EDGE,"E8");var subQ3=sQuery(id+"F2.wireOp",EDGE,"E7");var subQ4=makeQuery(id+"F5.opExtrude","CAP_FACE",FACE,{"disambiguationData":[OSD([subQ3,subQ2,subQ1,subQ0])],"isStart":false});var subQ5=makeQuery(id+"F8.opChamfer","BLEND_EDGE",EDGE,{"blendedFrom":[makeQuery(id+"F5.opExtrude","CAP_EDGE",EDGE,{"disambiguationData":[OSD([subQ0])],"isStart":false}),subQ4],"blendedInto":[subQ4]});var subQ6=makeQuery(id+"F9.opExtrude","CAP_EDGE",EDGE,{"disambiguationData":[OSD([subQ3,subQ2,subQ1,subQ0]),TDD([subQ5])],"isStart":false});Q1=makeQuery(id+"F26.opChamfer","BLEND_FACE",FACE,{"disambiguationData":[OSD([subQ3,subQ2,subQ1,subQ0]),TDD([makeQuery(id+"F25.opExtrude","SWEPT_EDGE",EDGE,{"disambiguationData":[OSD([subQ3,subQ2,subQ1,subQ0]),TDD([makeQuery(id+"F19.opExtrude","CAP_VERTEX",VERTEX,{"disambiguationData":[OSD([subQ3,subQ2,subQ1,subQ0]),TDD([makeQuery(id+"F17.opChamfer","BLEND_VERTEX",VERTEX,{"blendedFrom":[makeQuery(id+"F13.opExtrude","CAP_EDGE",EDGE,{"disambiguationData":[OSD([subQ3,subQ2,subQ1,subQ0]),TDD([makeQuery(id+"F10.opChamfer","BLEND_EDGE",EDGE,{"blendedFrom":[subQ6,makeQuery(id+"F9.opExtrude","SWEPT_FACE",FACE,{"disambiguationData":[OSD([subQ3,subQ2,subQ1,subQ0]),TDD([subQ5])]})],"blendedInto":[makeQuery(id+"F9.opExtrude","SWEPT_FACE",FACE,{"disambiguationData":[OSD([subQ3,subQ2,subQ1,subQ0]),TDD([subQ5])]})]})])],"isStart":false}),makeQuery(id+"F13.opExtrude","SWEPT_FACE",FACE,{"disambiguationData":[OSD([subQ3,subQ2,subQ1,subQ0]),TDD([makeQuery(id+"F10.opChamfer","BLEND_EDGE",EDGE,{"blendedFrom":[makeQuery(id+"F9.opExtrude","CAP_EDGE",EDGE,{"disambiguationData":[OSD([subQ3,subQ2,subQ1,subQ0]),TDD([makeQuery(id+"F8.opChamfer","BLEND_EDGE",EDGE,{"blendedFrom":[makeQuery(id+"F5.opExtrude","CAP_EDGE",EDGE,{"disambiguationData":[OSD([subQ3])],"isStart":false}),subQ4],"blendedInto":[subQ4]})])],"isStart":false}),subQ6],"blendedInto":[]})])]}),makeQuery(id+"F13.opExtrude","CAP_FACE",FACE,{"disambiguationData":[OSD([subQ3,subQ2,subQ1,subQ0]),TDD([makeQuery(id+"F10.opChamfer","BLEND_FACE",FACE,{"disambiguationData":[OSD([subQ3,subQ2,subQ1,subQ0]),TDD([subQ6])]})])],"isStart":false})],"blendedInto":[makeQuery(id+"F13.opExtrude","SWEPT_FACE",FACE,{"disambiguationData":[OSD([subQ3,subQ2,subQ1,subQ0]),TDD([makeQuery(id+"F10.opChamfer","BLEND_EDGE",EDGE,{"blendedFrom":[makeQuery(id+"F9.opExtrude","CAP_EDGE",EDGE,{"disambiguationData":[OSD([subQ3,subQ2,subQ1,subQ0]),TDD([makeQuery(id+"F8.opChamfer","BLEND_EDGE",EDGE,{"blendedFrom":[makeQuery(id+"F5.opExtrude","CAP_EDGE",EDGE,{"disambiguationData":[OSD([subQ3])],"isStart":false}),subQ4],"blendedInto":[subQ4]})])],"isStart":false}),subQ6],"blendedInto":[]})])]}),makeQuery(id+"F13.opExtrude","CAP_FACE",FACE,{"disambiguationData":[OSD([subQ3,subQ2,subQ1,subQ0]),TDD([makeQuery(id+"F10.opChamfer","BLEND_FACE",FACE,{"disambiguationData":[OSD([subQ3,subQ2,subQ1,subQ0]),TDD([subQ6])]})])],"isStart":false})]})])],"isStart":false})])]})])]});}
            var Q2;
            {var subQ0=sQuery(id+"F2.wireOp",EDGE,"E10");var subQ1=sQuery(id+"F2.wireOp",EDGE,"E9");var subQ2=sQuery(id+"F2.wireOp",EDGE,"E8");var subQ3=sQuery(id+"F2.wireOp",EDGE,"E7");var subQ4=makeQuery(id+"F9.opExtrude","CAP_FACE",FACE,{"disambiguationData":[OSD([subQ3,subQ2,subQ1,subQ0])],"isStart":false});var subQ5=makeQuery(id+"F5.opExtrude","CAP_FACE",FACE,{"disambiguationData":[OSD([subQ3,subQ2,subQ1,subQ0])],"isStart":false});var subQ6=makeQuery(id+"F10.opChamfer","BLEND_EDGE",EDGE,{"blendedFrom":[makeQuery(id+"F9.opExtrude","CAP_EDGE",EDGE,{"disambiguationData":[OSD([subQ3,subQ2,subQ1,subQ0]),TDD([makeQuery(id+"F8.opChamfer","BLEND_EDGE",EDGE,{"blendedFrom":[makeQuery(id+"F5.opExtrude","CAP_EDGE",EDGE,{"disambiguationData":[OSD([subQ0])],"isStart":false}),subQ5],"blendedInto":[subQ5]})])],"isStart":false}),subQ4],"blendedInto":[subQ4]});var subQ7=makeQuery(id+"F11.opExtrude","CAP_EDGE",EDGE,{"disambiguationData":[OSD([subQ3,subQ2,subQ1,subQ0]),TDD([subQ6])],"isStart":false});Q2=makeQuery(id+"F26.opChamfer","BLEND_FACE",FACE,{"disambiguationData":[OSD([subQ3,subQ2,subQ1,subQ0]),TDD([makeQuery(id+"F25.opExtrude","SWEPT_EDGE",EDGE,{"disambiguationData":[OSD([subQ3,subQ2,subQ1,subQ0]),TDD([makeQuery(id+"F19.opExtrude","CAP_VERTEX",VERTEX,{"disambiguationData":[OSD([subQ3,subQ2,subQ1,subQ0]),TDD([makeQuery(id+"F17.opChamfer","BLEND_VERTEX",VERTEX,{"blendedFrom":[makeQuery(id+"F13.opExtrude","CAP_EDGE",EDGE,{"disambiguationData":[OSD([subQ3,subQ2,subQ1,subQ0]),TDD([makeQuery(id+"F12.opChamfer","BLEND_EDGE",EDGE,{"blendedFrom":[subQ7,makeQuery(id+"F11.opExtrude","SWEPT_FACE",FACE,{"disambiguationData":[OSD([subQ3,subQ2,subQ1,subQ0]),TDD([subQ6])]})],"blendedInto":[makeQuery(id+"F11.opExtrude","SWEPT_FACE",FACE,{"disambiguationData":[OSD([subQ3,subQ2,subQ1,subQ0]),TDD([subQ6])]})]})])],"isStart":false}),makeQuery(id+"F13.opExtrude","SWEPT_FACE",FACE,{"disambiguationData":[OSD([subQ3,subQ2,subQ1,subQ0]),TDD([makeQuery(id+"F12.opChamfer","BLEND_EDGE",EDGE,{"blendedFrom":[makeQuery(id+"F11.opExtrude","CAP_EDGE",EDGE,{"disambiguationData":[OSD([subQ3,subQ2,subQ1,subQ0]),TDD([makeQuery(id+"F10.opChamfer","BLEND_EDGE",EDGE,{"blendedFrom":[makeQuery(id+"F9.opExtrude","CAP_EDGE",EDGE,{"disambiguationData":[OSD([subQ3,subQ2,subQ1,subQ0]),TDD([makeQuery(id+"F8.opChamfer","BLEND_EDGE",EDGE,{"blendedFrom":[makeQuery(id+"F5.opExtrude","CAP_EDGE",EDGE,{"disambiguationData":[OSD([subQ3])],"isStart":false}),subQ5],"blendedInto":[subQ5]})])],"isStart":false}),subQ4],"blendedInto":[subQ4]})])],"isStart":false}),subQ7],"blendedInto":[]})])]}),makeQuery(id+"F13.opExtrude","CAP_FACE",FACE,{"disambiguationData":[OSD([subQ3,subQ2,subQ1,subQ0]),TDD([makeQuery(id+"F12.opChamfer","BLEND_FACE",FACE,{"disambiguationData":[OSD([subQ3,subQ2,subQ1,subQ0]),TDD([subQ7])]})])],"isStart":false})],"blendedInto":[makeQuery(id+"F13.opExtrude","SWEPT_FACE",FACE,{"disambiguationData":[OSD([subQ3,subQ2,subQ1,subQ0]),TDD([makeQuery(id+"F12.opChamfer","BLEND_EDGE",EDGE,{"blendedFrom":[makeQuery(id+"F11.opExtrude","CAP_EDGE",EDGE,{"disambiguationData":[OSD([subQ3,subQ2,subQ1,subQ0]),TDD([makeQuery(id+"F10.opChamfer","BLEND_EDGE",EDGE,{"blendedFrom":[makeQuery(id+"F9.opExtrude","CAP_EDGE",EDGE,{"disambiguationData":[OSD([subQ3,subQ2,subQ1,subQ0]),TDD([makeQuery(id+"F8.opChamfer","BLEND_EDGE",EDGE,{"blendedFrom":[makeQuery(id+"F5.opExtrude","CAP_EDGE",EDGE,{"disambiguationData":[OSD([subQ3])],"isStart":false}),subQ5],"blendedInto":[subQ5]})])],"isStart":false}),subQ4],"blendedInto":[subQ4]})])],"isStart":false}),subQ7],"blendedInto":[]})])]}),makeQuery(id+"F13.opExtrude","CAP_FACE",FACE,{"disambiguationData":[OSD([subQ3,subQ2,subQ1,subQ0]),TDD([makeQuery(id+"F12.opChamfer","BLEND_FACE",FACE,{"disambiguationData":[OSD([subQ3,subQ2,subQ1,subQ0]),TDD([subQ7])]})])],"isStart":false})]})])],"isStart":false})])]})])]});}
            extrude(context, id + "F28", {"entities" : qUnion([Q0, Q1, Q2]), "operationType" : NewBodyOperationType.ADD, "depth" : 25.4 * mm});
        }
        {
            var Q0;
            {var subQ0=sQuery(id+"F2.wireOp",EDGE,"E10");var subQ1=sQuery(id+"F2.wireOp",EDGE,"E7");Q0=makeQuery(id+"F26.opChamfer","BLEND_FACE",FACE,{"disambiguationData":[OSD([subQ1,subQ0]),TDD([makeQuery(id+"F24.opExtrude","SWEPT_EDGE",EDGE,{"disambiguationData":[OSD([subQ1,subQ0]),TDD([makeQuery(id+"F20.opExtrude","CAP_VERTEX",VERTEX,{"disambiguationData":[OSD([subQ1,subQ0]),TDD([makeQuery(id+"F17.opChamfer","BLEND_VERTEX",VERTEX,{"blendedFrom":[makeQuery(id+"F15.opExtrude","CAP_EDGE",EDGE,{"disambiguationData":[OSD([subQ1])],"isStart":false}),makeQuery(id+"F15.opExtrude","CAP_FACE",FACE,{"disambiguationData":[OSD([subQ1])],"isStart":false}),makeQuery(id+"F15.opExtrude","SWEPT_FACE",FACE,{"disambiguationData":[OSD([subQ1,subQ0])]})],"blendedInto":[makeQuery(id+"F15.opExtrude","CAP_FACE",FACE,{"disambiguationData":[OSD([subQ1])],"isStart":false}),makeQuery(id+"F15.opExtrude","SWEPT_FACE",FACE,{"disambiguationData":[OSD([subQ1,subQ0])]})]})])],"isStart":false})])]})])]});}
            var Q1;
            {var subQ0=sQuery(id+"F2.wireOp",EDGE,"E10");var subQ1=sQuery(id+"F2.wireOp",EDGE,"E9");var subQ2=sQuery(id+"F2.wireOp",EDGE,"E8");var subQ3=sQuery(id+"F2.wireOp",EDGE,"E7");var subQ4=makeQuery(id+"F5.opExtrude","CAP_FACE",FACE,{"disambiguationData":[OSD([subQ3,subQ2,subQ1,subQ0])],"isStart":false});var subQ5=makeQuery(id+"F8.opChamfer","BLEND_EDGE",EDGE,{"blendedFrom":[makeQuery(id+"F5.opExtrude","CAP_EDGE",EDGE,{"disambiguationData":[OSD([subQ3])],"isStart":false}),subQ4],"blendedInto":[subQ4]});var subQ6=makeQuery(id+"F9.opExtrude","CAP_EDGE",EDGE,{"disambiguationData":[OSD([subQ3,subQ2,subQ1,subQ0]),TDD([subQ5])],"isStart":false});var subQ7=makeQuery(id+"F10.opChamfer","BLEND_EDGE",EDGE,{"blendedFrom":[subQ6,makeQuery(id+"F9.opExtrude","CAP_EDGE",EDGE,{"disambiguationData":[OSD([subQ3,subQ2,subQ1,subQ0]),TDD([makeQuery(id+"F8.opChamfer","BLEND_EDGE",EDGE,{"blendedFrom":[makeQuery(id+"F5.opExtrude","CAP_EDGE",EDGE,{"disambiguationData":[OSD([subQ0])],"isStart":false}),subQ4],"blendedInto":[subQ4]})])],"isStart":false})],"blendedInto":[]});Q1=makeQuery(id+"F26.opChamfer","BLEND_FACE",FACE,{"disambiguationData":[OSD([subQ3,subQ2,subQ1,subQ0]),TDD([makeQuery(id+"F24.opExtrude","SWEPT_EDGE",EDGE,{"disambiguationData":[OSD([subQ3,subQ2,subQ1,subQ0]),TDD([makeQuery(id+"F20.opExtrude","CAP_VERTEX",VERTEX,{"disambiguationData":[OSD([subQ3,subQ2,subQ1,subQ0]),TDD([makeQuery(id+"F17.opChamfer","BLEND_VERTEX",VERTEX,{"blendedFrom":[makeQuery(id+"F15.opExtrude","CAP_EDGE",EDGE,{"disambiguationData":[OSD([subQ3,subQ2,subQ1,subQ0]),TDD([makeQuery(id+"F10.opChamfer","BLEND_EDGE",EDGE,{"blendedFrom":[subQ6,makeQuery(id+"F9.opExtrude","SWEPT_FACE",FACE,{"disambiguationData":[OSD([subQ3,subQ2,subQ1,subQ0]),TDD([subQ5])]})],"blendedInto":[makeQuery(id+"F9.opExtrude","SWEPT_FACE",FACE,{"disambiguationData":[OSD([subQ3,subQ2,subQ1,subQ0]),TDD([subQ5])]})]})])],"isStart":false}),makeQuery(id+"F15.opExtrude","CAP_FACE",FACE,{"disambiguationData":[OSD([subQ3,subQ2,subQ1,subQ0]),TDD([makeQuery(id+"F10.opChamfer","BLEND_FACE",FACE,{"disambiguationData":[OSD([subQ3,subQ2,subQ1,subQ0]),TDD([subQ6])]})])],"isStart":false}),makeQuery(id+"F15.opExtrude","SWEPT_FACE",FACE,{"disambiguationData":[OSD([subQ3,subQ2,subQ1,subQ0]),TDD([makeQuery(id+"F13.boolean.opBoolean","MERGE",EDGE,{"derivedFrom":[subQ7,makeQuery(id+"F13.opExtrude","CAP_EDGE",EDGE,{"disambiguationData":[OSD([subQ3,subQ2,subQ1,subQ0]),TDD([subQ7])],"isStart":true})]})])]})],"blendedInto":[makeQuery(id+"F15.opExtrude","CAP_FACE",FACE,{"disambiguationData":[OSD([subQ3,subQ2,subQ1,subQ0]),TDD([makeQuery(id+"F10.opChamfer","BLEND_FACE",FACE,{"disambiguationData":[OSD([subQ3,subQ2,subQ1,subQ0]),TDD([subQ6])]})])],"isStart":false}),makeQuery(id+"F15.opExtrude","SWEPT_FACE",FACE,{"disambiguationData":[OSD([subQ3,subQ2,subQ1,subQ0]),TDD([makeQuery(id+"F13.boolean.opBoolean","MERGE",EDGE,{"derivedFrom":[subQ7,makeQuery(id+"F13.opExtrude","CAP_EDGE",EDGE,{"disambiguationData":[OSD([subQ3,subQ2,subQ1,subQ0]),TDD([subQ7])],"isStart":true})]})])]})]})])],"isStart":false})])]})])]});}
            var Q2;
            {var subQ0=sQuery(id+"F2.wireOp",EDGE,"E10");var subQ1=sQuery(id+"F2.wireOp",EDGE,"E9");var subQ2=sQuery(id+"F2.wireOp",EDGE,"E8");var subQ3=sQuery(id+"F2.wireOp",EDGE,"E7");var subQ4=makeQuery(id+"F9.opExtrude","CAP_FACE",FACE,{"disambiguationData":[OSD([subQ3,subQ2,subQ1,subQ0])],"isStart":false});var subQ5=makeQuery(id+"F5.opExtrude","CAP_FACE",FACE,{"disambiguationData":[OSD([subQ3,subQ2,subQ1,subQ0])],"isStart":false});var subQ6=makeQuery(id+"F10.opChamfer","BLEND_EDGE",EDGE,{"blendedFrom":[makeQuery(id+"F9.opExtrude","CAP_EDGE",EDGE,{"disambiguationData":[OSD([subQ3,subQ2,subQ1,subQ0]),TDD([makeQuery(id+"F8.opChamfer","BLEND_EDGE",EDGE,{"blendedFrom":[makeQuery(id+"F5.opExtrude","CAP_EDGE",EDGE,{"disambiguationData":[OSD([subQ3])],"isStart":false}),subQ5],"blendedInto":[subQ5]})])],"isStart":false}),subQ4],"blendedInto":[subQ4]});var subQ7=makeQuery(id+"F11.opExtrude","CAP_EDGE",EDGE,{"disambiguationData":[OSD([subQ3,subQ2,subQ1,subQ0]),TDD([subQ6])],"isStart":false});var subQ8=makeQuery(id+"F12.opChamfer","BLEND_EDGE",EDGE,{"blendedFrom":[subQ7,makeQuery(id+"F11.opExtrude","CAP_EDGE",EDGE,{"disambiguationData":[OSD([subQ3,subQ2,subQ1,subQ0]),TDD([makeQuery(id+"F10.opChamfer","BLEND_EDGE",EDGE,{"blendedFrom":[makeQuery(id+"F9.opExtrude","CAP_EDGE",EDGE,{"disambiguationData":[OSD([subQ3,subQ2,subQ1,subQ0]),TDD([makeQuery(id+"F8.opChamfer","BLEND_EDGE",EDGE,{"blendedFrom":[makeQuery(id+"F5.opExtrude","CAP_EDGE",EDGE,{"disambiguationData":[OSD([subQ0])],"isStart":false}),subQ5],"blendedInto":[subQ5]})])],"isStart":false}),subQ4],"blendedInto":[subQ4]})])],"isStart":false})],"blendedInto":[]});Q2=makeQuery(id+"F26.opChamfer","BLEND_FACE",FACE,{"disambiguationData":[OSD([subQ3,subQ2,subQ1,subQ0]),TDD([makeQuery(id+"F24.opExtrude","SWEPT_EDGE",EDGE,{"disambiguationData":[OSD([subQ3,subQ2,subQ1,subQ0]),TDD([makeQuery(id+"F20.opExtrude","CAP_VERTEX",VERTEX,{"disambiguationData":[OSD([subQ3,subQ2,subQ1,subQ0]),TDD([makeQuery(id+"F17.opChamfer","BLEND_VERTEX",VERTEX,{"blendedFrom":[makeQuery(id+"F15.opExtrude","CAP_EDGE",EDGE,{"disambiguationData":[OSD([subQ3,subQ2,subQ1,subQ0]),TDD([makeQuery(id+"F12.opChamfer","BLEND_EDGE",EDGE,{"blendedFrom":[subQ7,makeQuery(id+"F11.opExtrude","SWEPT_FACE",FACE,{"disambiguationData":[OSD([subQ3,subQ2,subQ1,subQ0]),TDD([subQ6])]})],"blendedInto":[makeQuery(id+"F11.opExtrude","SWEPT_FACE",FACE,{"disambiguationData":[OSD([subQ3,subQ2,subQ1,subQ0]),TDD([subQ6])]})]})])],"isStart":false}),makeQuery(id+"F15.opExtrude","CAP_FACE",FACE,{"disambiguationData":[OSD([subQ3,subQ2,subQ1,subQ0]),TDD([makeQuery(id+"F12.opChamfer","BLEND_FACE",FACE,{"disambiguationData":[OSD([subQ3,subQ2,subQ1,subQ0]),TDD([subQ7])]})])],"isStart":false}),makeQuery(id+"F15.opExtrude","SWEPT_FACE",FACE,{"disambiguationData":[OSD([subQ3,subQ2,subQ1,subQ0]),TDD([makeQuery(id+"F13.boolean.opBoolean","MERGE",EDGE,{"derivedFrom":[subQ8,makeQuery(id+"F13.opExtrude","CAP_EDGE",EDGE,{"disambiguationData":[OSD([subQ3,subQ2,subQ1,subQ0]),TDD([subQ8])],"isStart":true})]})])]})],"blendedInto":[makeQuery(id+"F15.opExtrude","CAP_FACE",FACE,{"disambiguationData":[OSD([subQ3,subQ2,subQ1,subQ0]),TDD([makeQuery(id+"F12.opChamfer","BLEND_FACE",FACE,{"disambiguationData":[OSD([subQ3,subQ2,subQ1,subQ0]),TDD([subQ7])]})])],"isStart":false}),makeQuery(id+"F15.opExtrude","SWEPT_FACE",FACE,{"disambiguationData":[OSD([subQ3,subQ2,subQ1,subQ0]),TDD([makeQuery(id+"F13.boolean.opBoolean","MERGE",EDGE,{"derivedFrom":[subQ8,makeQuery(id+"F13.opExtrude","CAP_EDGE",EDGE,{"disambiguationData":[OSD([subQ3,subQ2,subQ1,subQ0]),TDD([subQ8])],"isStart":true})]})])]})]})])],"isStart":false})])]})])]});}
            extrude(context, id + "F29", {"entities" : qUnion([Q0, Q1, Q2]), "operationType" : NewBodyOperationType.ADD, "depth" : 25.4 * mm});
        }
        {
            var Q0;
            {var subQ0=sQuery(id+"F2.wireOp",EDGE,"E9");var subQ1=sQuery(id+"F2.wireOp",EDGE,"E8");Q0=makeQuery(id+"F26.opChamfer","BLEND_FACE",FACE,{"disambiguationData":[OSD([subQ1,subQ0]),TDD([makeQuery(id+"F23.opExtrude","SWEPT_EDGE",EDGE,{"disambiguationData":[OSD([subQ1,subQ0]),TDD([makeQuery(id+"F21.opExtrude","CAP_VERTEX",VERTEX,{"disambiguationData":[OSD([subQ1,subQ0]),TDD([makeQuery(id+"F17.opChamfer","BLEND_VERTEX",VERTEX,{"blendedFrom":[makeQuery(id+"F16.opExtrude","CAP_EDGE",EDGE,{"disambiguationData":[OSD([subQ1])],"isStart":false}),makeQuery(id+"F16.opExtrude","CAP_FACE",FACE,{"disambiguationData":[OSD([subQ1])],"isStart":false}),makeQuery(id+"F16.opExtrude","SWEPT_FACE",FACE,{"disambiguationData":[OSD([subQ1,subQ0])]})],"blendedInto":[makeQuery(id+"F16.opExtrude","CAP_FACE",FACE,{"disambiguationData":[OSD([subQ1])],"isStart":false}),makeQuery(id+"F16.opExtrude","SWEPT_FACE",FACE,{"disambiguationData":[OSD([subQ1,subQ0])]})]})])],"isStart":false})])]})])]});}
            var Q1;
            {var subQ0=sQuery(id+"F2.wireOp",EDGE,"E10");var subQ1=sQuery(id+"F2.wireOp",EDGE,"E9");var subQ2=sQuery(id+"F2.wireOp",EDGE,"E8");var subQ3=sQuery(id+"F2.wireOp",EDGE,"E7");var subQ4=makeQuery(id+"F5.opExtrude","CAP_FACE",FACE,{"disambiguationData":[OSD([subQ3,subQ2,subQ1,subQ0])],"isStart":false});var subQ5=makeQuery(id+"F8.opChamfer","BLEND_EDGE",EDGE,{"blendedFrom":[makeQuery(id+"F5.opExtrude","CAP_EDGE",EDGE,{"disambiguationData":[OSD([subQ2])],"isStart":false}),subQ4],"blendedInto":[subQ4]});var subQ6=makeQuery(id+"F9.opExtrude","CAP_EDGE",EDGE,{"disambiguationData":[OSD([subQ3,subQ2,subQ1,subQ0]),TDD([subQ5])],"isStart":false});var subQ7=makeQuery(id+"F10.opChamfer","BLEND_EDGE",EDGE,{"blendedFrom":[subQ6,makeQuery(id+"F9.opExtrude","CAP_EDGE",EDGE,{"disambiguationData":[OSD([subQ3,subQ2,subQ1,subQ0]),TDD([makeQuery(id+"F8.opChamfer","BLEND_EDGE",EDGE,{"blendedFrom":[makeQuery(id+"F5.opExtrude","CAP_EDGE",EDGE,{"disambiguationData":[OSD([subQ1])],"isStart":false}),subQ4],"blendedInto":[subQ4]})])],"isStart":false})],"blendedInto":[]});Q1=makeQuery(id+"F26.opChamfer","BLEND_FACE",FACE,{"disambiguationData":[OSD([subQ3,subQ2,subQ1,subQ0]),TDD([makeQuery(id+"F23.opExtrude","SWEPT_EDGE",EDGE,{"disambiguationData":[OSD([subQ3,subQ2,subQ1,subQ0]),TDD([makeQuery(id+"F21.opExtrude","CAP_VERTEX",VERTEX,{"disambiguationData":[OSD([subQ3,subQ2,subQ1,subQ0]),TDD([makeQuery(id+"F17.opChamfer","BLEND_VERTEX",VERTEX,{"blendedFrom":[makeQuery(id+"F16.opExtrude","CAP_EDGE",EDGE,{"disambiguationData":[OSD([subQ3,subQ2,subQ1,subQ0]),TDD([makeQuery(id+"F10.opChamfer","BLEND_EDGE",EDGE,{"blendedFrom":[subQ6,makeQuery(id+"F9.opExtrude","SWEPT_FACE",FACE,{"disambiguationData":[OSD([subQ3,subQ2,subQ1,subQ0]),TDD([subQ5])]})],"blendedInto":[makeQuery(id+"F9.opExtrude","SWEPT_FACE",FACE,{"disambiguationData":[OSD([subQ3,subQ2,subQ1,subQ0]),TDD([subQ5])]})]})])],"isStart":false}),makeQuery(id+"F16.opExtrude","CAP_FACE",FACE,{"disambiguationData":[OSD([subQ3,subQ2,subQ1,subQ0]),TDD([makeQuery(id+"F10.opChamfer","BLEND_FACE",FACE,{"disambiguationData":[OSD([subQ3,subQ2,subQ1,subQ0]),TDD([subQ6])]})])],"isStart":false}),makeQuery(id+"F16.opExtrude","SWEPT_FACE",FACE,{"disambiguationData":[OSD([subQ3,subQ2,subQ1,subQ0]),TDD([makeQuery(id+"F14.boolean.opBoolean","MERGE",EDGE,{"derivedFrom":[subQ7,makeQuery(id+"F14.opExtrude","CAP_EDGE",EDGE,{"disambiguationData":[OSD([subQ3,subQ2,subQ1,subQ0]),TDD([subQ7])],"isStart":true})]})])]})],"blendedInto":[makeQuery(id+"F16.opExtrude","CAP_FACE",FACE,{"disambiguationData":[OSD([subQ3,subQ2,subQ1,subQ0]),TDD([makeQuery(id+"F10.opChamfer","BLEND_FACE",FACE,{"disambiguationData":[OSD([subQ3,subQ2,subQ1,subQ0]),TDD([subQ6])]})])],"isStart":false}),makeQuery(id+"F16.opExtrude","SWEPT_FACE",FACE,{"disambiguationData":[OSD([subQ3,subQ2,subQ1,subQ0]),TDD([makeQuery(id+"F14.boolean.opBoolean","MERGE",EDGE,{"derivedFrom":[subQ7,makeQuery(id+"F14.opExtrude","CAP_EDGE",EDGE,{"disambiguationData":[OSD([subQ3,subQ2,subQ1,subQ0]),TDD([subQ7])],"isStart":true})]})])]})]})])],"isStart":false})])]})])]});}
            var Q2;
            {var subQ0=sQuery(id+"F2.wireOp",EDGE,"E10");var subQ1=sQuery(id+"F2.wireOp",EDGE,"E9");var subQ2=sQuery(id+"F2.wireOp",EDGE,"E8");var subQ3=sQuery(id+"F2.wireOp",EDGE,"E7");var subQ4=makeQuery(id+"F9.opExtrude","CAP_FACE",FACE,{"disambiguationData":[OSD([subQ3,subQ2,subQ1,subQ0])],"isStart":false});var subQ5=makeQuery(id+"F5.opExtrude","CAP_FACE",FACE,{"disambiguationData":[OSD([subQ3,subQ2,subQ1,subQ0])],"isStart":false});var subQ6=makeQuery(id+"F10.opChamfer","BLEND_EDGE",EDGE,{"blendedFrom":[makeQuery(id+"F9.opExtrude","CAP_EDGE",EDGE,{"disambiguationData":[OSD([subQ3,subQ2,subQ1,subQ0]),TDD([makeQuery(id+"F8.opChamfer","BLEND_EDGE",EDGE,{"blendedFrom":[makeQuery(id+"F5.opExtrude","CAP_EDGE",EDGE,{"disambiguationData":[OSD([subQ2])],"isStart":false}),subQ5],"blendedInto":[subQ5]})])],"isStart":false}),subQ4],"blendedInto":[subQ4]});var subQ7=makeQuery(id+"F11.opExtrude","CAP_EDGE",EDGE,{"disambiguationData":[OSD([subQ3,subQ2,subQ1,subQ0]),TDD([subQ6])],"isStart":false});var subQ8=makeQuery(id+"F12.opChamfer","BLEND_EDGE",EDGE,{"blendedFrom":[subQ7,makeQuery(id+"F11.opExtrude","CAP_EDGE",EDGE,{"disambiguationData":[OSD([subQ3,subQ2,subQ1,subQ0]),TDD([makeQuery(id+"F10.opChamfer","BLEND_EDGE",EDGE,{"blendedFrom":[makeQuery(id+"F9.opExtrude","CAP_EDGE",EDGE,{"disambiguationData":[OSD([subQ3,subQ2,subQ1,subQ0]),TDD([makeQuery(id+"F8.opChamfer","BLEND_EDGE",EDGE,{"blendedFrom":[makeQuery(id+"F5.opExtrude","CAP_EDGE",EDGE,{"disambiguationData":[OSD([subQ1])],"isStart":false}),subQ5],"blendedInto":[subQ5]})])],"isStart":false}),subQ4],"blendedInto":[subQ4]})])],"isStart":false})],"blendedInto":[]});Q2=makeQuery(id+"F26.opChamfer","BLEND_FACE",FACE,{"disambiguationData":[OSD([subQ3,subQ2,subQ1,subQ0]),TDD([makeQuery(id+"F23.opExtrude","SWEPT_EDGE",EDGE,{"disambiguationData":[OSD([subQ3,subQ2,subQ1,subQ0]),TDD([makeQuery(id+"F21.opExtrude","CAP_VERTEX",VERTEX,{"disambiguationData":[OSD([subQ3,subQ2,subQ1,subQ0]),TDD([makeQuery(id+"F17.opChamfer","BLEND_VERTEX",VERTEX,{"blendedFrom":[makeQuery(id+"F16.opExtrude","CAP_EDGE",EDGE,{"disambiguationData":[OSD([subQ3,subQ2,subQ1,subQ0]),TDD([makeQuery(id+"F12.opChamfer","BLEND_EDGE",EDGE,{"blendedFrom":[subQ7,makeQuery(id+"F11.opExtrude","SWEPT_FACE",FACE,{"disambiguationData":[OSD([subQ3,subQ2,subQ1,subQ0]),TDD([subQ6])]})],"blendedInto":[makeQuery(id+"F11.opExtrude","SWEPT_FACE",FACE,{"disambiguationData":[OSD([subQ3,subQ2,subQ1,subQ0]),TDD([subQ6])]})]})])],"isStart":false}),makeQuery(id+"F16.opExtrude","CAP_FACE",FACE,{"disambiguationData":[OSD([subQ3,subQ2,subQ1,subQ0]),TDD([makeQuery(id+"F12.opChamfer","BLEND_FACE",FACE,{"disambiguationData":[OSD([subQ3,subQ2,subQ1,subQ0]),TDD([subQ7])]})])],"isStart":false}),makeQuery(id+"F16.opExtrude","SWEPT_FACE",FACE,{"disambiguationData":[OSD([subQ3,subQ2,subQ1,subQ0]),TDD([makeQuery(id+"F14.boolean.opBoolean","MERGE",EDGE,{"derivedFrom":[subQ8,makeQuery(id+"F14.opExtrude","CAP_EDGE",EDGE,{"disambiguationData":[OSD([subQ3,subQ2,subQ1,subQ0]),TDD([subQ8])],"isStart":true})]})])]})],"blendedInto":[makeQuery(id+"F16.opExtrude","CAP_FACE",FACE,{"disambiguationData":[OSD([subQ3,subQ2,subQ1,subQ0]),TDD([makeQuery(id+"F12.opChamfer","BLEND_FACE",FACE,{"disambiguationData":[OSD([subQ3,subQ2,subQ1,subQ0]),TDD([subQ7])]})])],"isStart":false}),makeQuery(id+"F16.opExtrude","SWEPT_FACE",FACE,{"disambiguationData":[OSD([subQ3,subQ2,subQ1,subQ0]),TDD([makeQuery(id+"F14.boolean.opBoolean","MERGE",EDGE,{"derivedFrom":[subQ8,makeQuery(id+"F14.opExtrude","CAP_EDGE",EDGE,{"disambiguationData":[OSD([subQ3,subQ2,subQ1,subQ0]),TDD([subQ8])],"isStart":true})]})])]})]})])],"isStart":false})])]})])]});}
            extrude(context, id + "F30", {"entities" : qUnion([Q0, Q1, Q2]), "operationType" : NewBodyOperationType.ADD, "depth" : 25.4 * mm});
        }
    });
